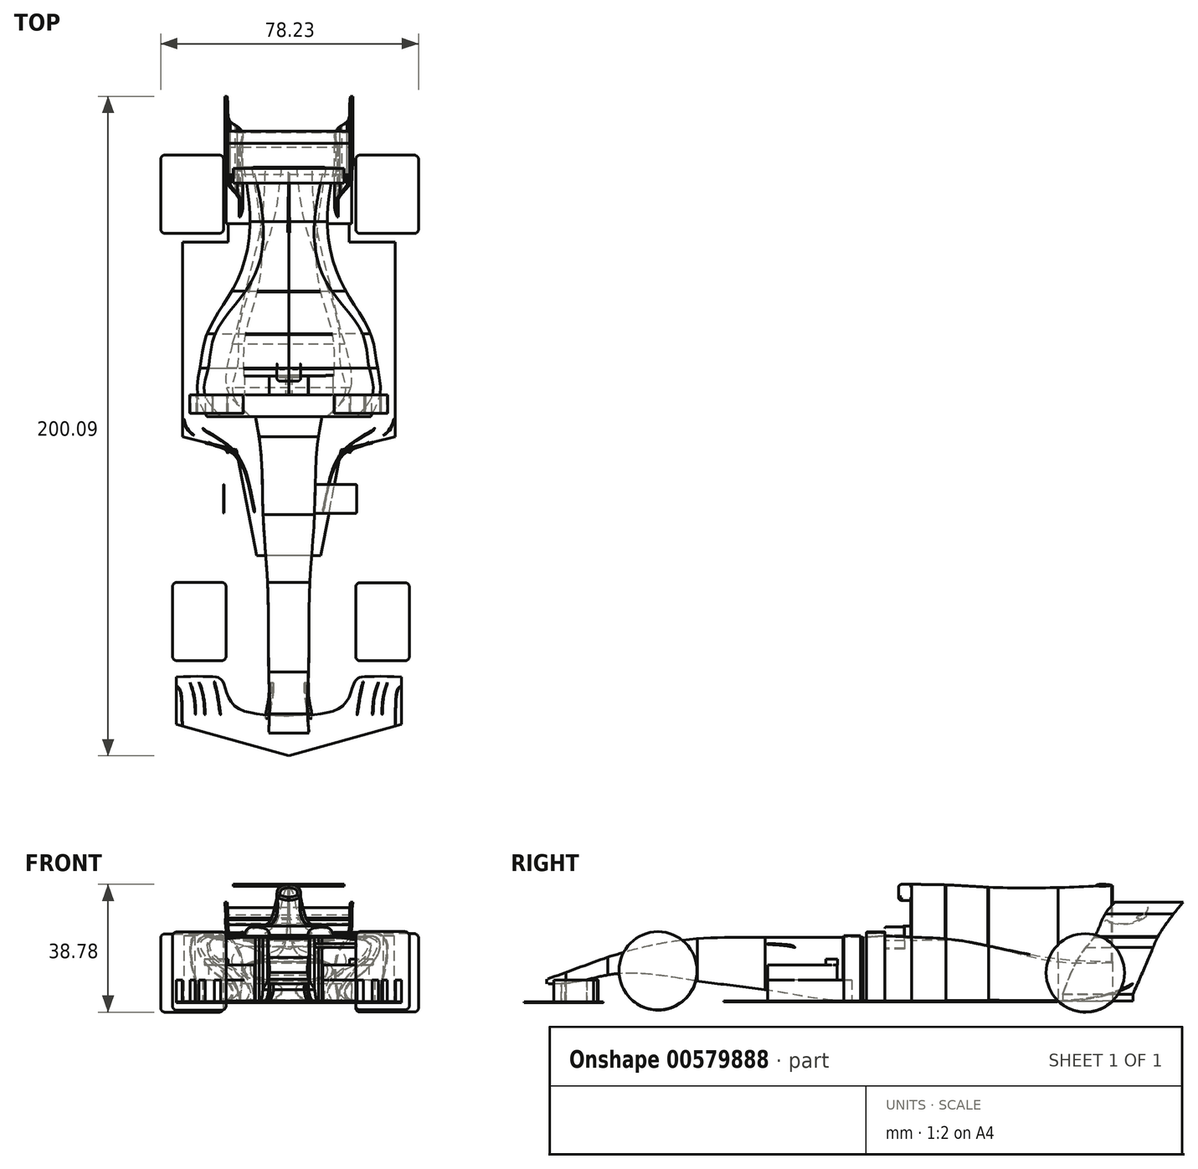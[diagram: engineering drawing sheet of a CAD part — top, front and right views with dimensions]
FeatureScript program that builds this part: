
annotation { "Feature Type Name" : "Feature", "Feature Type Description" : "" }
export const myFeature = defineFeature(function(context is Context, id is Id, definition is map)
    precondition{}
    {
        {
            var Q0;
            Q0=qCreatedBy(makeId("Top.planeOp"),FACE);
            cPlane(context, id + "F0", {"entities" : qUnion([Q0]), "cplaneType" : CPlaneType.OFFSET, "offset" : 1.52 * mm, "width" : 152.4 * mm, "height" : 152.4 * mm});
        }
        {
            var Q0;
            Q0=qCreatedBy(id+"F0.planeOp",FACE);
            var sketch = newSketch(context, id + "F1", { "sketchPlane" : qUnion([Q0])});
            skLineSegment(sketch, "E0", {"start": v(0, -36.14) * mm, "end": v(9.74, -36.14) * mm});
            skLineSegment(sketch, "E1", {"start": v(9.74, -36.14) * mm, "end": v(15.88, -3.95) * mm});
            skLineSegment(sketch, "E2", {"start": v(15.88, -3.95) * mm, "end": v(32.24, 0) * mm});
            skLineSegment(sketch, "E3", {"start": v(32.24, 0) * mm, "end": v(32.24, 59.05) * mm});
            skLineSegment(sketch, "E4", {"start": v(32.24, 59.05) * mm, "end": v(18.33, 59.05) * mm});
            skLineSegment(sketch, "E5", {"start": v(18.33, 59.05) * mm, "end": v(18.33, 64.56) * mm});
            skLineSegment(sketch, "E6", {"start": v(18.33, 64.56) * mm, "end": v(0, 64.56) * mm});
            skLineSegment(sketch, "E7.MirrorCS", {"start": v(-18.33, 64.56) * mm, "end": v(0, 64.56) * mm});
            skLineSegment(sketch, "E8.MirrorCS", {"start": v(-18.33, 59.05) * mm, "end": v(-18.33, 64.56) * mm});
            skLineSegment(sketch, "E9.MirrorCS", {"start": v(-32.24, 59.05) * mm, "end": v(-18.33, 59.05) * mm});
            skLineSegment(sketch, "E10.MirrorCS", {"start": v(-32.24, 0) * mm, "end": v(-32.24, 59.05) * mm});
            skLineSegment(sketch, "E11.MirrorCS", {"start": v(-15.88, -3.95) * mm, "end": v(-32.24, 0) * mm});
            skLineSegment(sketch, "E12.MirrorCS", {"start": v(-9.74, -36.14) * mm, "end": v(-15.88, -3.95) * mm});
            skLineSegment(sketch, "E13.MirrorCS", {"start": v(0, -36.14) * mm, "end": v(-9.74, -36.14) * mm});
            skSolve(sketch);
        }
        {
            var Q0;
            Q0 = qSketchRegion(id + "F1", true);
            extrude(context, id + "F2", {"entities" : qUnion([Q0]), "depth" : 0.25 * mm, "offsetDistance" : 25.4 * mm});
        }
        {
            var Q0;
            Q0=qCreatedBy(makeId("Front.planeOp"),FACE);
            cPlane(context, id + "F3", {"entities" : qUnion([Q0]), "cplaneType" : CPlaneType.OFFSET, "offset" : 6.1 * mm, "oppositeDirection" : true, "width" : 152.4 * mm, "height" : 152.4 * mm});
        }
        {
            var Q0;
            Q0=qCreatedBy(id+"F3.planeOp",FACE);
            var sketch = newSketch(context, id + "F4", { "sketchPlane" : qUnion([Q0])});
            skLineSegment(sketch, "E14", {"start": v(0, 21.08) * mm, "end": v(-20.66, 21.08) * mm});
            skFitSpline(sketch, "E15", {"points": [v(-20.66, 21.08) * mm, v(-24.08, 20.42) * mm, v(-24.53, 17.17) * mm, v(-20.66, 13.07) * mm, v(-17.24, 11.22) * mm, v(-12.52, 6.88) * mm, v(-11.6, 3.37) * mm, v(-11.6, 1.83) * mm], "startDerivative": vector(-14.07, -2.12) * mm, "endDerivative": vector(0, -19.5) * mm});
            skLineSegment(sketch, "E16", {"start": v(-11.6, 1.83) * mm, "end": v(0, 1.83) * mm});
            skLineSegment(sketch, "E17.MirrorCS", {"start": v(11.6, 1.83) * mm, "end": v(0, 1.83) * mm});
            skFitSpline(sketch, "E18.MirrorCS", {"points": [v(20.66, 21.08) * mm, v(24.08, 20.42) * mm, v(24.53, 17.17) * mm, v(20.66, 13.07) * mm, v(17.24, 11.22) * mm, v(12.52, 6.88) * mm, v(11.6, 3.37) * mm, v(11.6, 1.83) * mm], "startDerivative": vector(14.07, -2.12) * mm, "endDerivative": vector(0, -19.5) * mm});
            skLineSegment(sketch, "E19.MirrorCS", {"start": v(0, 21.08) * mm, "end": v(20.66, 21.08) * mm});
            skSolve(sketch);
        }
        {
            var Q0;
            Q0=qCreatedBy(makeId("Front.planeOp"),FACE);
            cPlane(context, id + "F5", {"entities" : qUnion([Q0]), "cplaneType" : CPlaneType.OFFSET, "offset" : 12.7 * mm, "oppositeDirection" : true, "width" : 152.4 * mm, "height" : 152.4 * mm});
        }
        {
            var Q0;
            Q0=qCreatedBy(id+"F5.planeOp",FACE);
            var sketch = newSketch(context, id + "F6", { "sketchPlane" : qUnion([Q0])});
            skLineSegment(sketch, "E20", {"start": v(0, 21.43) * mm, "end": v(-25.43, 21.43) * mm});
            skFitSpline(sketch, "E21", {"points": [v(-25.43, 21.43) * mm, v(-27.4, 19.99) * mm, v(-26.9, 15.65) * mm, v(-25.16, 13.06) * mm, v(-22.6, 10.51) * mm, v(-17.72, 6.46) * mm, v(-17.04, 3.68) * mm, v(-17.85, 1.8) * mm], "startDerivative": vector(-11.51, -2.68) * mm, "endDerivative": vector(-12.74, -13.46) * mm});
            skLineSegment(sketch, "E22.MirrorCS", {"start": v(0, 21.43) * mm, "end": v(25.43, 21.43) * mm});
            skFitSpline(sketch, "E23.MirrorCS", {"points": [v(25.43, 21.43) * mm, v(27.4, 19.99) * mm, v(26.9, 15.65) * mm, v(25.16, 13.06) * mm, v(22.6, 10.51) * mm, v(17.72, 6.46) * mm, v(17.04, 3.68) * mm, v(17.85, 1.8) * mm], "startDerivative": vector(11.51, -2.68) * mm, "endDerivative": vector(12.74, -13.46) * mm});
            skLineSegment(sketch, "E24", {"start": v(-17.85, 1.8) * mm, "end": v(0, 1.8) * mm});
            skLineSegment(sketch, "E25.MirrorCS", {"start": v(17.85, 1.8) * mm, "end": v(0, 1.8) * mm});
            skSolve(sketch);
        }
        {
            var Q0;
            Q0=qCreatedBy(makeId("Front.planeOp"),FACE);
            cPlane(context, id + "F7", {"entities" : qUnion([Q0]), "cplaneType" : CPlaneType.OFFSET, "offset" : 20.83 * mm, "oppositeDirection" : true, "width" : 152.4 * mm, "height" : 152.4 * mm});
        }
        {
            var Q0;
            Q0=qCreatedBy(id+"F7.planeOp",FACE);
            var sketch = newSketch(context, id + "F8", { "sketchPlane" : qUnion([Q0])});
            skLineSegment(sketch, "E26", {"start": v(0, 21.13) * mm, "end": v(-24.43, 21.13) * mm});
            skFitSpline(sketch, "E27", {"points": [v(-24.43, 21.13) * mm, v(-26.8, 19.6) * mm, v(-25.78, 15.83) * mm, v(-24.43, 14.33) * mm, v(-21.34, 11.76) * mm, v(-17.18, 7.5) * mm, v(-15.86, 3.52) * mm, v(-18.92, 1.72) * mm], "startDerivative": vector(-13.1, -3.81) * mm, "endDerivative": vector(-24.59, -10.93) * mm});
            skLineSegment(sketch, "E28", {"start": v(-18.92, 1.72) * mm, "end": v(0, 1.72) * mm});
            skLineSegment(sketch, "E29.MirrorCS", {"start": v(0, 21.13) * mm, "end": v(24.43, 21.13) * mm});
            skFitSpline(sketch, "E30.MirrorCS", {"points": [v(24.43, 21.13) * mm, v(26.8, 19.6) * mm, v(25.78, 15.83) * mm, v(24.43, 14.33) * mm, v(21.34, 11.76) * mm, v(17.18, 7.5) * mm, v(15.86, 3.52) * mm, v(18.92, 1.72) * mm], "startDerivative": vector(13.1, -3.81) * mm, "endDerivative": vector(24.59, -10.93) * mm});
            skLineSegment(sketch, "E31.MirrorCS", {"start": v(18.92, 1.72) * mm, "end": v(0, 1.72) * mm});
            skSolve(sketch);
        }
        {
            var Q0;
            Q0=qCreatedBy(makeId("Front.planeOp"),FACE);
            cPlane(context, id + "F9", {"entities" : qUnion([Q0]), "cplaneType" : CPlaneType.OFFSET, "offset" : 31.24 * mm, "oppositeDirection" : true, "width" : 152.4 * mm, "height" : 152.4 * mm});
        }
        {
            var Q0;
            Q0=qCreatedBy(id+"F9.planeOp",FACE);
            var sketch = newSketch(context, id + "F10", { "sketchPlane" : qUnion([Q0])});
            skLineSegment(sketch, "E32", {"start": v(0, 20.64) * mm, "end": v(-22.4, 20.64) * mm});
            skFitSpline(sketch, "E33", {"points": [v(-22.4, 20.64) * mm, v(-24.53, 18.88) * mm, v(-24.28, 15.63) * mm, v(-22.8, 13.69) * mm, v(-20.83, 12.1) * mm, v(-16.57, 7.67) * mm, v(-15.37, 3.35) * mm, v(-16.12, 1.82) * mm], "startDerivative": vector(-10.02, -1.64) * mm, "endDerivative": vector(-7.67, -10.3) * mm});
            skLineSegment(sketch, "E34", {"start": v(-16.12, 1.82) * mm, "end": v(0, 1.82) * mm});
            skLineSegment(sketch, "E35.MirrorCS", {"start": v(0, 20.64) * mm, "end": v(22.4, 20.64) * mm});
            skFitSpline(sketch, "E36.MirrorCS", {"points": [v(22.4, 20.64) * mm, v(24.53, 18.88) * mm, v(24.28, 15.63) * mm, v(22.8, 13.69) * mm, v(20.83, 12.1) * mm, v(16.57, 7.67) * mm, v(15.37, 3.35) * mm, v(16.12, 1.82) * mm], "startDerivative": vector(10.02, -1.64) * mm, "endDerivative": vector(7.67, -10.3) * mm});
            skLineSegment(sketch, "E37.MirrorCS", {"start": v(16.12, 1.82) * mm, "end": v(0, 1.82) * mm});
            skSolve(sketch);
        }
        {
            var Q0;
            Q0=qCreatedBy(makeId("Front.planeOp"),FACE);
            cPlane(context, id + "F11", {"entities" : qUnion([Q0]), "cplaneType" : CPlaneType.OFFSET, "offset" : 44.2 * mm, "oppositeDirection" : true, "width" : 152.4 * mm, "height" : 152.4 * mm});
        }
        {
            var Q0;
            Q0=qCreatedBy(makeId("Front.planeOp"),FACE);
            cPlane(context, id + "F12", {"entities" : qUnion([Q0]), "cplaneType" : CPlaneType.OFFSET, "offset" : 65.28 * mm, "oppositeDirection" : true, "width" : 152.4 * mm, "height" : 152.4 * mm});
        }
        {
            var Q0;
            Q0=qCreatedBy(id+"F12.planeOp",FACE);
            var sketch = newSketch(context, id + "F13", { "sketchPlane" : qUnion([Q0])});
            skLineSegment(sketch, "E38", {"start": v(0, 14.58) * mm, "end": v(-7.82, 14.58) * mm});
            skFitSpline(sketch, "E39", {"points": [v(-7.82, 14.58) * mm, v(-11.15, 12.99) * mm, v(-11.62, 10.56) * mm, v(-10.8, 9.03) * mm, v(-7.82, 7.78) * mm, v(-4.75, 6.13) * mm, v(-6.17, 3.06) * mm, v(-8.2, 1.83) * mm], "startDerivative": vector(-13.2, -1) * mm, "endDerivative": vector(-13.85, -8.87) * mm});
            skLineSegment(sketch, "E40", {"start": v(-8.2, 1.83) * mm, "end": v(0, 1.83) * mm});
            skLineSegment(sketch, "E41.MirrorCS", {"start": v(0, 14.58) * mm, "end": v(7.82, 14.58) * mm});
            skFitSpline(sketch, "E42.MirrorCS", {"points": [v(7.82, 14.58) * mm, v(11.15, 12.99) * mm, v(11.62, 10.56) * mm, v(10.8, 9.03) * mm, v(7.82, 7.78) * mm, v(4.75, 6.13) * mm, v(6.17, 3.06) * mm, v(8.2, 1.83) * mm], "startDerivative": vector(13.2, -1) * mm, "endDerivative": vector(13.85, -8.87) * mm});
            skLineSegment(sketch, "E43.MirrorCS", {"start": v(8.2, 1.83) * mm, "end": v(0, 1.83) * mm});
            skSolve(sketch);
        }
        {
            var Q0;
            Q0=qCreatedBy(id+"F11.planeOp",FACE);
            var sketch = newSketch(context, id + "F14", { "sketchPlane" : qUnion([Q0])});
            skLineSegment(sketch, "E44", {"start": v(0, 18.43) * mm, "end": v(-13.07, 18.43) * mm});
            skFitSpline(sketch, "E45", {"points": [v(-13.07, 18.43) * mm, v(-16.95, 15.5) * mm, v(-16.64, 11.23) * mm, v(-14.93, 9.11) * mm, v(-13.61, 7.75) * mm, v(-12.5, 6.19) * mm, v(-12.15, 3.76) * mm, v(-13.04, 1.94) * mm], "startDerivative": vector(-21.24, 0.66) * mm, "endDerivative": vector(-6.74, -11.7) * mm});
            skLineSegment(sketch, "E46", {"start": v(-13.04, 1.94) * mm, "end": v(0, 1.94) * mm});
            skFitSpline(sketch, "E47.MirrorCS", {"points": [v(13.07, 18.43) * mm, v(16.95, 15.5) * mm, v(16.64, 11.23) * mm, v(14.93, 9.11) * mm, v(13.61, 7.75) * mm, v(12.5, 6.19) * mm, v(12.15, 3.76) * mm, v(13.04, 1.94) * mm], "startDerivative": vector(21.24, 0.66) * mm, "endDerivative": vector(6.74, -11.7) * mm});
            skLineSegment(sketch, "E48.MirrorCS", {"start": v(0, 18.43) * mm, "end": v(13.07, 18.43) * mm});
            skLineSegment(sketch, "E49.MirrorCS", {"start": v(13.04, 1.94) * mm, "end": v(0, 1.94) * mm});
            skSolve(sketch);
        }
        {
            var Q0;
            Q0=qCreatedBy(makeId("Front.planeOp"),FACE);
            cPlane(context, id + "F15", {"entities" : qUnion([Q0]), "cplaneType" : CPlaneType.OFFSET, "offset" : 81.8 * mm, "oppositeDirection" : true, "width" : 152.4 * mm, "height" : 152.4 * mm});
        }
        {
            var Q0;
            Q0=qCreatedBy(id+"F15.planeOp",FACE);
            var sketch = newSketch(context, id + "F16", { "sketchPlane" : qUnion([Q0])});
            skLineSegment(sketch, "E50", {"start": v(0, 13.69) * mm, "end": v(-10.77, 13.69) * mm});
            skFitSpline(sketch, "E51", {"points": [v(-10.77, 13.69) * mm, v(-12.3, 13.22) * mm, v(-13.7, 11.27) * mm, v(-12.76, 9.24) * mm, v(-10.22, 8.52) * mm, v(-3.54, 7.08) * mm, v(-2.77, 3.5) * mm, v(-7.08, 1.82) * mm], "startDerivative": vector(-13.13, -1.96) * mm, "endDerivative": vector(-9.84, -12.7) * mm});
            skLineSegment(sketch, "E52", {"start": v(-7.08, 1.82) * mm, "end": v(0, 1.82) * mm});
            skLineSegment(sketch, "E53.MirrorCS", {"start": v(0, 13.69) * mm, "end": v(10.77, 13.69) * mm});
            skFitSpline(sketch, "E54.MirrorCS", {"points": [v(10.77, 13.69) * mm, v(12.3, 13.22) * mm, v(13.7, 11.27) * mm, v(12.76, 9.24) * mm, v(10.22, 8.52) * mm, v(3.54, 7.08) * mm, v(2.77, 3.5) * mm, v(7.08, 1.82) * mm], "startDerivative": vector(13.13, -1.96) * mm, "endDerivative": vector(9.84, -12.7) * mm});
            skLineSegment(sketch, "E55.MirrorCS", {"start": v(7.08, 1.82) * mm, "end": v(0, 1.82) * mm});
            skSolve(sketch);
        }
        {
            var Q0;
            Q0 = qSketchRegion(id + "F16", true);
            var Q1;
            Q1 = qSketchRegion(id + "F14", true);
            var Q2;
            Q2 = qSketchRegion(id + "F13", true);
            var Q3;
            Q3 = qSketchRegion(id + "F10", true);
            var Q4;
            Q4 = qSketchRegion(id + "F8", true);
            var Q5;
            Q5 = qSketchRegion(id + "F6", true);
            var Q6;
            Q6 = qSketchRegion(id + "F4", true);
            extrude(context, id + "F17", {"entities" : qUnion([Q0, Q1, Q2, Q3, Q4, Q5, Q6]), "depth" : 0.03 * mm, "offsetDistance" : 25.4 * mm});
        }
        {
            var Q0;
            Q0=makeQuery(id+"F4.imprint","IMPRINT",FACE,{"disambiguationData":[TD([[makeQuery(id+"F4.imprint","IMPRINT",EDGE,{"derivedFrom":sQuery(id+"F4.wireOp",EDGE,"E14")}),1.0]])]});
            var Q1;
            Q1=makeQuery(id+"F6.imprint","IMPRINT",FACE,{"disambiguationData":[TD([[makeQuery(id+"F6.imprint","IMPRINT",EDGE,{"derivedFrom":sQuery(id+"F6.wireOp",EDGE,"E20")}),1.0]])]});
            var Q2;
            Q2=makeQuery(id+"F8.imprint","IMPRINT",FACE,{"disambiguationData":[TD([[makeQuery(id+"F8.imprint","IMPRINT",EDGE,{"derivedFrom":sQuery(id+"F8.wireOp",EDGE,"E26")}),1.0]])]});
            var Q3;
            Q3=makeQuery(id+"F10.imprint","IMPRINT",FACE,{"disambiguationData":[TD([[makeQuery(id+"F10.imprint","IMPRINT",EDGE,{"derivedFrom":sQuery(id+"F10.wireOp",EDGE,"E32")}),1.0]])]});
            var Q4;
            Q4=makeQuery(id+"F14.imprint","IMPRINT",FACE,{"disambiguationData":[TD([[makeQuery(id+"F14.imprint","IMPRINT",EDGE,{"derivedFrom":sQuery(id+"F14.wireOp",EDGE,"E44")}),1.0]])]});
            var Q5;
            Q5=makeQuery(id+"F13.imprint","IMPRINT",FACE,{"disambiguationData":[TD([[makeQuery(id+"F13.imprint","IMPRINT",EDGE,{"derivedFrom":sQuery(id+"F13.wireOp",EDGE,"E38")}),1.0]])]});
            var Q6;
            Q6=makeQuery(id+"F16.imprint","IMPRINT",FACE,{"disambiguationData":[TD([[makeQuery(id+"F16.imprint","IMPRINT",EDGE,{"derivedFrom":sQuery(id+"F16.wireOp",EDGE,"E50")}),1.0]])]});
            loft(context, id + "F18", {"sheetProfilesArray" : [{ "sheetProfileEntities" : qUnion([Q0]) }, { "sheetProfileEntities" : qUnion([Q1]) }, { "sheetProfileEntities" : qUnion([Q2]) }, { "sheetProfileEntities" : qUnion([Q3]) }, { "sheetProfileEntities" : qUnion([Q4]) }, { "sheetProfileEntities" : qUnion([Q5]) }, { "sheetProfileEntities" : qUnion([Q6]) }]});
        }
        {
            var Q0;
            Q0=qCreatedBy(makeId("Right.planeOp"),FACE);
            cPlane(context, id + "F19", {"entities" : qUnion([Q0]), "cplaneType" : CPlaneType.OFFSET, "offset" : 20.32 * mm, "width" : 152.4 * mm, "height" : 152.4 * mm});
        }
        {
            var Q0;
            Q0=qCreatedBy(makeId("Right.planeOp"),FACE);
            cPlane(context, id + "F20", {"entities" : qUnion([Q0]), "cplaneType" : CPlaneType.OFFSET, "offset" : 19.8 * mm, "oppositeDirection" : true, "width" : 152.4 * mm, "height" : 152.4 * mm});
        }
        {
            var Q0;
            Q0=qCreatedBy(id+"F19.planeOp",FACE);
            var sketch = newSketch(context, id + "F21", { "sketchPlane" : qUnion([Q0])});
            skCircle(sketch, "E56", {"center": v(73.53, 10.3) * mm, "radius": 11.88 * mm});
            skSolve(sketch);
        }
        {
            var Q0;
            Q0=qCreatedBy(id+"F20.planeOp",FACE);
            var sketch = newSketch(context, id + "F22", { "sketchPlane" : qUnion([Q0])});
            skCircle(sketch, "E57", {"center": v(73.58, 10.23) * mm, "radius": 11.86 * mm});
            skSolve(sketch);
        }
        {
            var Q0;
            Q0 = qSketchRegion(id + "F22", true);
            extrude(context, id + "F23", {"entities" : qUnion([Q0]), "oppositeDirection" : true, "depth" : 19.05 * mm, "offsetDistance" : 25.4 * mm});
        }
        {
            var Q0;
            Q0=makeQuery(id+"F21.imprint","IMPRINT",FACE,{"disambiguationData":[TD([[makeQuery(id+"F21.imprint","IMPRINT",EDGE,{"derivedFrom":sQuery(id+"F21.wireOp",EDGE,"E56")}),1.0]])]});
            extrude(context, id + "F24", {"entities" : qUnion([Q0]), "depth" : 19.05 * mm, "offsetDistance" : 25.4 * mm});
        }
        {
            var Q0;
            Q0=qCreatedBy(id+"F5.planeOp",FACE);
            var sketch = newSketch(context, id + "F25", { "sketchPlane" : qUnion([Q0])});
            skLineSegment(sketch, "E58", {"start": v(-14.07, 21.3) * mm, "end": v(-14.07, 22.26) * mm});
            skLineSegment(sketch, "E59", {"start": v(-14.07, 21.3) * mm, "end": v(-13.76, 21.3) * mm});
            skLineSegment(sketch, "E60", {"start": v(-13.76, 21.3) * mm, "end": v(-13.76, 22.26) * mm});
            skLineSegment(sketch, "E61", {"start": v(-14.07, 22.26) * mm, "end": v(-18.39, 22.26) * mm});
            skLineSegment(sketch, "E62", {"start": v(-18.39, 22.26) * mm, "end": v(-18.39, 21.15) * mm});
            skLineSegment(sketch, "E63", {"start": v(-18.39, 21.15) * mm, "end": v(-18.72, 21.15) * mm});
            skLineSegment(sketch, "E64", {"start": v(-18.72, 21.15) * mm, "end": v(-18.72, 22.26) * mm});
            skLineSegment(sketch, "E65", {"start": v(-18.72, 22.26) * mm, "end": v(-22.91, 22.26) * mm});
            skLineSegment(sketch, "E66", {"start": v(-22.91, 22.26) * mm, "end": v(-22.91, 21.15) * mm});
            skLineSegment(sketch, "E67", {"start": v(-22.91, 21.15) * mm, "end": v(-23.25, 21.15) * mm});
            skLineSegment(sketch, "E68", {"start": v(-23.25, 21.15) * mm, "end": v(-23.25, 22.26) * mm});
            skLineSegment(sketch, "E69", {"start": v(-23.25, 22.26) * mm, "end": v(-25.19, 22.26) * mm});
            skFitSpline(sketch, "E70", {"points": [v(-13.76, 22.26) * mm, v(-13.89, 22.61) * mm, v(-14.18, 22.63) * mm, v(-17, 22.6) * mm, v(-25.25, 22.6) * mm, v(-26.09, 22.58) * mm, v(-26.89, 22.47) * mm, v(-27.43, 22.26) * mm, v(-28.64, 21.5) * mm, v(-29.89, 19.12) * mm, v(-29.92, 16.38) * mm, v(-29.53, 12.69) * mm, v(-28.55, 8.5) * mm, v(-27.98, 4.57) * mm, v(-28.07, 1.78) * mm], "startDerivative": vector(-5.07, 15.17) * mm, "endDerivative": vector(-2.51, -33.45) * mm});
            skFitSpline(sketch, "E71", {"points": [v(-25.19, 22.26) * mm, v(-25.88, 22.26) * mm, v(-27.32, 21.92) * mm, v(-28.28, 21.35) * mm, v(-29.14, 20.12) * mm, v(-29.62, 18.68) * mm, v(-29.6, 16.32) * mm, v(-29.17, 12.69) * mm, v(-28.34, 8.97) * mm, v(-27.77, 6.04) * mm, v(-27.65, 3.07) * mm, v(-27.7, 1.75) * mm], "startDerivative": vector(-11.42, 0.46) * mm, "endDerivative": vector(-1.02, -15.85) * mm});
            skLineSegment(sketch, "E72", {"start": v(-28.07, 1.78) * mm, "end": v(-27.7, 1.75) * mm});
            skFitSpline(sketch, "E73.MirrorCS", {"points": [v(13.76, 22.26) * mm, v(13.89, 22.61) * mm, v(14.18, 22.63) * mm, v(17, 22.6) * mm, v(25.25, 22.6) * mm, v(26.09, 22.58) * mm, v(26.89, 22.47) * mm, v(27.43, 22.26) * mm, v(28.64, 21.5) * mm, v(29.89, 19.12) * mm, v(29.92, 16.38) * mm, v(29.53, 12.69) * mm, v(28.55, 8.5) * mm, v(27.98, 4.57) * mm, v(28.07, 1.78) * mm], "startDerivative": vector(5.07, 15.17) * mm, "endDerivative": vector(2.51, -33.45) * mm});
            skLineSegment(sketch, "E74.MirrorCS", {"start": v(14.07, 22.26) * mm, "end": v(18.39, 22.26) * mm});
            skLineSegment(sketch, "E75.MirrorCS", {"start": v(14.07, 21.3) * mm, "end": v(14.07, 22.26) * mm});
            skLineSegment(sketch, "E76.MirrorCS", {"start": v(13.76, 21.3) * mm, "end": v(13.76, 22.26) * mm});
            skLineSegment(sketch, "E77.MirrorCS", {"start": v(14.07, 21.3) * mm, "end": v(13.76, 21.3) * mm});
            skLineSegment(sketch, "E78.MirrorCS", {"start": v(18.39, 22.26) * mm, "end": v(18.39, 21.15) * mm});
            skLineSegment(sketch, "E79.MirrorCS", {"start": v(18.39, 21.15) * mm, "end": v(18.72, 21.15) * mm});
            skLineSegment(sketch, "E80.MirrorCS", {"start": v(18.72, 21.15) * mm, "end": v(18.72, 22.26) * mm});
            skLineSegment(sketch, "E81.MirrorCS", {"start": v(18.72, 22.26) * mm, "end": v(22.91, 22.26) * mm});
            skFitSpline(sketch, "E82.MirrorCS", {"points": [v(25.19, 22.26) * mm, v(25.88, 22.26) * mm, v(27.32, 21.92) * mm, v(28.28, 21.35) * mm, v(29.14, 20.12) * mm, v(29.62, 18.68) * mm, v(29.6, 16.32) * mm, v(29.17, 12.69) * mm, v(28.34, 8.97) * mm, v(27.77, 6.04) * mm, v(27.65, 3.07) * mm, v(27.7, 1.75) * mm], "startDerivative": vector(11.42, 0.46) * mm, "endDerivative": vector(1.02, -15.85) * mm});
            skLineSegment(sketch, "E83.MirrorCS", {"start": v(23.25, 22.26) * mm, "end": v(25.19, 22.26) * mm});
            skLineSegment(sketch, "E84.MirrorCS", {"start": v(23.25, 21.15) * mm, "end": v(23.25, 22.26) * mm});
            skLineSegment(sketch, "E85.MirrorCS", {"start": v(22.91, 22.26) * mm, "end": v(22.91, 21.15) * mm});
            skLineSegment(sketch, "E86.MirrorCS", {"start": v(22.91, 21.15) * mm, "end": v(23.25, 21.15) * mm});
            skLineSegment(sketch, "E87.MirrorCS", {"start": v(-11.56, 1.78) * mm, "end": v(-11.92, 1.75) * mm});
            skLineSegment(sketch, "E88", {"start": v(27.7, 1.75) * mm, "end": v(28.07, 1.78) * mm});
            skSolve(sketch);
        }
        {
            var Q0;
            Q0 = qSketchRegion(id + "F25", true);
            extrude(context, id + "F26", {"entities" : qUnion([Q0]), "operationType" : NewBodyOperationType.ADD, "depth" : 5.6 * mm, "offsetDistance" : 25.4 * mm});
        }
        {
            var Q0;
            Q0=makeQuery(id+"F24.opExtrude","CAP_EDGE",EDGE,{"disambiguationData":[OSD([sQuery(id+"F21.wireOp",EDGE,"E56")])],"isStart":false});
            fillet(context, id + "F27", {"entities" : qUnion([Q0]), "radius" : 1.27 * mm, "tangentPropagation" : true, "allowEdgeOverflow" : false});
        }
        {
            var Q0;
            Q0=makeQuery(id+"F24.opExtrude","CAP_EDGE",EDGE,{"disambiguationData":[OSD([sQuery(id+"F21.wireOp",EDGE,"E56")])],"isStart":true});
            fillet(context, id + "F28", {"entities" : qUnion([Q0]), "radius" : 1.27 * mm, "tangentPropagation" : true, "allowEdgeOverflow" : false});
        }
        {
            var Q0;
            Q0=makeQuery(id+"F23.opExtrude","CAP_EDGE",EDGE,{"disambiguationData":[OSD([sQuery(id+"F22.wireOp",EDGE,"E57")])],"isStart":true});
            fillet(context, id + "F29", {"entities" : qUnion([Q0]), "radius" : 1.27 * mm, "tangentPropagation" : true, "allowEdgeOverflow" : false});
        }
        {
            var Q0;
            Q0=makeQuery(id+"F23.opExtrude","CAP_EDGE",EDGE,{"disambiguationData":[OSD([sQuery(id+"F22.wireOp",EDGE,"E57")])],"isStart":false});
            fillet(context, id + "F30", {"entities" : qUnion([Q0]), "radius" : 1.27 * mm, "tangentPropagation" : true, "allowEdgeOverflow" : false});
        }
        {
            var Q0;
            Q0=makeQuery(id+"F2.opExtrude","CAP_FACE",FACE,{"disambiguationData":[OSD([sQuery(id+"F1.wireOp",EDGE,"E0"),sQuery(id+"F1.wireOp",EDGE,"E1"),sQuery(id+"F1.wireOp",EDGE,"E2"),sQuery(id+"F1.wireOp",EDGE,"E3"),sQuery(id+"F1.wireOp",EDGE,"E4"),sQuery(id+"F1.wireOp",EDGE,"E5"),sQuery(id+"F1.wireOp",EDGE,"E6"),sQuery(id+"F1.wireOp",EDGE,"E7.MirrorCS"),sQuery(id+"F1.wireOp",EDGE,"E8.MirrorCS"),sQuery(id+"F1.wireOp",EDGE,"E9.MirrorCS"),sQuery(id+"F1.wireOp",EDGE,"E10.MirrorCS"),sQuery(id+"F1.wireOp",EDGE,"E11.MirrorCS"),sQuery(id+"F1.wireOp",EDGE,"E12.MirrorCS"),sQuery(id+"F1.wireOp",EDGE,"E13.MirrorCS")])],"isStart":false});
            var sketch = newSketch(context, id + "F31", { "sketchPlane" : qUnion([Q0])});
            skLineSegment(sketch, "E89", {"start": v(-15.07, 66.68) * mm, "end": v(-15.07, 87.96) * mm});
            skLineSegment(sketch, "E90", {"start": v(-15.07, 87.96) * mm, "end": v(-14.7, 87.96) * mm});
            skLineSegment(sketch, "E91", {"start": v(-14.7, 87.96) * mm, "end": v(-14.7, 66.68) * mm});
            skLineSegment(sketch, "E92", {"start": v(-14.7, 66.68) * mm, "end": v(-15.07, 66.68) * mm});
            skLineSegment(sketch, "E93.MirrorCS", {"start": v(15.07, 66.68) * mm, "end": v(15.07, 87.96) * mm});
            skLineSegment(sketch, "E94.MirrorCS", {"start": v(14.7, 87.96) * mm, "end": v(14.7, 66.68) * mm});
            skLineSegment(sketch, "E95.MirrorCS", {"start": v(15.07, 87.96) * mm, "end": v(14.7, 87.96) * mm});
            skLineSegment(sketch, "E96.MirrorCS", {"start": v(14.7, 66.68) * mm, "end": v(15.07, 66.68) * mm});
            skSolve(sketch);
        }
        {
            var Q0;
            Q0 = qSketchRegion(id + "F31", true);
            extrude(context, id + "F32", {"entities" : qUnion([Q0]), "operationType" : NewBodyOperationType.ADD, "depth" : 2.03 * mm, "offsetDistance" : 25.4 * mm});
        }
        {
            var Q0;
            Q0=qCreatedBy(makeId("Top.planeOp"),FACE);
            cPlane(context, id + "F33", {"entities" : qUnion([Q0]), "cplaneType" : CPlaneType.OFFSET, "offset" : 18.03 * mm, "width" : 152.4 * mm, "height" : 152.4 * mm});
        }
        {
            var Q0;
            Q0=qCreatedBy(makeId("Top.planeOp"),FACE);
            cPlane(context, id + "F34", {"entities" : qUnion([Q0]), "cplaneType" : CPlaneType.OFFSET, "offset" : 21.34 * mm, "width" : 152.4 * mm, "height" : 152.4 * mm});
        }
        {
            var Q0;
            Q0=qCreatedBy(makeId("Top.planeOp"),FACE);
            cPlane(context, id + "F35", {"entities" : qUnion([Q0]), "cplaneType" : CPlaneType.OFFSET, "offset" : 28.2 * mm, "width" : 152.4 * mm, "height" : 152.4 * mm});
        }
        {
            var Q0;
            Q0=qCreatedBy(id+"F33.planeOp",FACE);
            var sketch = newSketch(context, id + "F36", { "sketchPlane" : qUnion([Q0])});
            skLineSegment(sketch, "E97", {"start": v(-15.6, 73.75) * mm, "end": v(-15.6, 94.13) * mm});
            skLineSegment(sketch, "E98", {"start": v(-16.16, 73.75) * mm, "end": v(-15.6, 73.75) * mm});
            skLineSegment(sketch, "E99", {"start": v(-16.16, 73.75) * mm, "end": v(-16.16, 94.13) * mm});
            skLineSegment(sketch, "E100", {"start": v(-15.6, 94.13) * mm, "end": v(-16.16, 94.13) * mm});
            skLineSegment(sketch, "E101.MirrorCS", {"start": v(16.16, 73.75) * mm, "end": v(16.16, 94.13) * mm});
            skLineSegment(sketch, "E102.MirrorCS", {"start": v(15.6, 73.75) * mm, "end": v(15.6, 94.13) * mm});
            skLineSegment(sketch, "E103.MirrorCS", {"start": v(15.6, 94.13) * mm, "end": v(16.16, 94.13) * mm});
            skLineSegment(sketch, "E104.MirrorCS", {"start": v(16.16, 73.75) * mm, "end": v(15.6, 73.75) * mm});
            skSolve(sketch);
        }
        {
            var Q0;
            Q0 = qSketchRegion(id + "F36", true);
            extrude(context, id + "F37", {"entities" : qUnion([Q0]), "oppositeDirection" : true, "depth" : 0.03 * mm, "offsetDistance" : 25.4 * mm});
        }
        {
            var Q0;
            Q0=qCreatedBy(id+"F34.planeOp",FACE);
            var sketch = newSketch(context, id + "F38", { "sketchPlane" : qUnion([Q0])});
            skLineSegment(sketch, "E105", {"start": v(-17.72, 76.4) * mm, "end": v(-18.44, 76.4) * mm});
            skLineSegment(sketch, "E106", {"start": v(-17.72, 76.4) * mm, "end": v(-17.72, 95.6) * mm});
            skLineSegment(sketch, "E107", {"start": v(-18.47, 95.6) * mm, "end": v(-17.72, 95.6) * mm});
            skLineSegment(sketch, "E108", {"start": v(-18.47, 95.6) * mm, "end": v(-18.44, 76.4) * mm});
            skLineSegment(sketch, "E109.MirrorCS", {"start": v(18.47, 95.6) * mm, "end": v(18.44, 76.4) * mm});
            skLineSegment(sketch, "E110.MirrorCS", {"start": v(17.72, 76.4) * mm, "end": v(17.72, 95.6) * mm});
            skLineSegment(sketch, "E111.MirrorCS", {"start": v(18.47, 95.6) * mm, "end": v(17.72, 95.6) * mm});
            skLineSegment(sketch, "E112.MirrorCS", {"start": v(17.72, 76.4) * mm, "end": v(18.44, 76.4) * mm});
            skSolve(sketch);
        }
        {
            var Q0;
            Q0 = qSketchRegion(id + "F38", true);
            extrude(context, id + "F39", {"entities" : qUnion([Q0]), "oppositeDirection" : true, "depth" : 0.25 * mm, "offsetDistance" : 25.4 * mm});
        }
        {
            var Q0;
            Q0=qCreatedBy(id+"F35.planeOp",FACE);
            var sketch = newSketch(context, id + "F40", { "sketchPlane" : qUnion([Q0])});
            skLineSegment(sketch, "E113", {"start": v(-19.18, 79.55) * mm, "end": v(-18.47, 79.55) * mm});
            skLineSegment(sketch, "E114", {"start": v(-18.47, 79.55) * mm, "end": v(-18.47, 100.35) * mm});
            skLineSegment(sketch, "E115", {"start": v(-18.47, 100.35) * mm, "end": v(-19.04, 100.35) * mm});
            skLineSegment(sketch, "E116", {"start": v(-19.04, 100.35) * mm, "end": v(-19.18, 79.55) * mm});
            skLineSegment(sketch, "E117.MirrorCS", {"start": v(19.04, 100.35) * mm, "end": v(19.18, 79.55) * mm});
            skLineSegment(sketch, "E118.MirrorCS", {"start": v(18.47, 79.55) * mm, "end": v(18.47, 100.35) * mm});
            skLineSegment(sketch, "E119.MirrorCS", {"start": v(18.47, 100.35) * mm, "end": v(19.04, 100.35) * mm});
            skLineSegment(sketch, "E120.MirrorCS", {"start": v(19.18, 79.55) * mm, "end": v(18.47, 79.55) * mm});
            skSolve(sketch);
        }
        {
            var Q0;
            Q0 = qSketchRegion(id + "F40", true);
            extrude(context, id + "F41", {"entities" : qUnion([Q0]), "oppositeDirection" : true, "depth" : 0.03 * mm, "offsetDistance" : 25.4 * mm});
        }
        {
            var Q0;
            Q0=qCreatedBy(makeId("Right.planeOp"),FACE);
            cPlane(context, id + "F42", {"entities" : qUnion([Q0]), "cplaneType" : CPlaneType.OFFSET, "offset" : 19.05 * mm, "oppositeDirection" : true, "width" : 152.4 * mm, "height" : 152.4 * mm});
        }
        {
            var Q0;
            Q0=qCreatedBy(id+"F42.planeOp",FACE);
            var sketch = newSketch(context, id + "F43", { "sketchPlane" : qUnion([Q0])});
            skFitSpline(sketch, "E121", {"points": [v(79.72, 25.92) * mm, v(79.48, 26.13) * mm, v(79.57, 26.33) * mm, v(79.83, 26.37) * mm, v(80.49, 26.1) * mm, v(81.36, 25.8) * mm, v(83.23, 25.36) * mm, v(86.13, 25.33) * mm, v(87.67, 25.63) * mm, v(91.21, 27.08) * mm, v(92.19, 27.76) * mm, v(92.11, 27.44) * mm, v(90.46, 26.26) * mm, v(88.41, 25.46) * mm, v(86.37, 25) * mm, v(83.05, 24.99) * mm, v(80.22, 25.68) * mm, v(79.72, 25.92) * mm]});
            skFitSpline(sketch, "E122", {"points": [v(90.8, 27.94) * mm, v(89.1, 27.16) * mm, v(89.03, 26.95) * mm, v(89.31, 26.9) * mm, v(89.94, 27.05) * mm, v(90.57, 27.3) * mm, v(91.51, 28) * mm, v(92.37, 29.12) * mm, v(92.64, 29.8) * mm, v(92.62, 30.08) * mm, v(92.4, 29.97) * mm, v(92.28, 29.78) * mm, v(90.8, 27.94) * mm]});
            skSolve(sketch);
        }
        {
            var Q0;
            Q0 = qSketchRegion(id + "F43", true);
            extrude(context, id + "F44", {"entities" : qUnion([Q0]), "depth" : 38.15 * mm, "offsetDistance" : 25.4 * mm});
        }
        {
            var Q0;
            Q0=qCreatedBy(id+"F7.planeOp",FACE);
            var sketch = newSketch(context, id + "F45", { "sketchPlane" : qUnion([Q0])});
            skFitSpline(sketch, "E123", {"points": [v(-13.78, 20) * mm, v(-12.44, 23.67) * mm, v(-5.54, 25.03) * mm, v(-3.54, 32.27) * mm, v(0.06, 37.14) * mm], "startDerivative": vector(5.54, 13.24) * mm, "endDerivative": vector(49.3, 3.23) * mm});
            skLineSegment(sketch, "E124", {"start": v(-13.78, 20) * mm, "end": v(0.09, 20) * mm});
            skFitSpline(sketch, "E125.MirrorCS", {"points": [v(13.78, 20) * mm, v(12.44, 23.67) * mm, v(5.54, 25.03) * mm, v(3.54, 32.27) * mm, v(-0.06, 37.14) * mm], "startDerivative": vector(-5.54, 13.24) * mm, "endDerivative": vector(-49.3, 3.23) * mm});
            skLineSegment(sketch, "E126.MirrorCS", {"start": v(13.78, 20) * mm, "end": v(-0.09, 20) * mm});
            skSolve(sketch);
        }
        {
            var Q0;
            Q0=qCreatedBy(id+"F9.planeOp",FACE);
            var sketch = newSketch(context, id + "F46", { "sketchPlane" : qUnion([Q0])});
            skLineSegment(sketch, "E127", {"start": v(-13.2, 20.14) * mm, "end": v(0, 20.14) * mm});
            skFitSpline(sketch, "E128", {"points": [v(-13.2, 20.14) * mm, v(-12.06, 23.15) * mm, v(-6.31, 25.33) * mm, v(-2.93, 34.94) * mm, v(0.05, 36.99) * mm], "startDerivative": vector(4.36, 13.73) * mm, "endDerivative": vector(15.44, 0.81) * mm});
            skFitSpline(sketch, "E129.MirrorCS", {"points": [v(13.2, 20.14) * mm, v(12.06, 23.15) * mm, v(6.31, 25.33) * mm, v(2.93, 34.94) * mm, v(-0.05, 36.99) * mm], "startDerivative": vector(-4.36, 13.73) * mm, "endDerivative": vector(-15.44, 0.81) * mm});
            skLineSegment(sketch, "E130.MirrorCS", {"start": v(13.2, 20.14) * mm, "end": v(0, 20.14) * mm});
            skSolve(sketch);
        }
        {
            var Q0;
            Q0=qCreatedBy(id+"F11.planeOp",FACE);
            var sketch = newSketch(context, id + "F47", { "sketchPlane" : qUnion([Q0])});
            skLineSegment(sketch, "E131", {"start": v(-9.6, 18.32) * mm, "end": v(0.02, 18.32) * mm});
            skFitSpline(sketch, "E132", {"points": [v(-9.6, 18.32) * mm, v(-7.06, 22.29) * mm, v(-4.17, 24.78) * mm, v(-1.71, 33.12) * mm, v(0.05, 36.3) * mm], "startDerivative": vector(26.07, 15.07) * mm, "endDerivative": vector(11.26, 0.63) * mm});
            skFitSpline(sketch, "E133.MirrorCS", {"points": [v(9.6, 18.32) * mm, v(7.06, 22.29) * mm, v(4.17, 24.78) * mm, v(1.71, 33.12) * mm, v(-0.05, 36.3) * mm], "startDerivative": vector(-26.07, 15.07) * mm, "endDerivative": vector(-11.26, 0.63) * mm});
            skLineSegment(sketch, "E134.MirrorCS", {"start": v(9.6, 18.32) * mm, "end": v(-0.02, 18.32) * mm});
            skSolve(sketch);
        }
        {
            var Q0;
            Q0=qCreatedBy(id+"F15.planeOp",FACE);
            var sketch = newSketch(context, id + "F48", { "sketchPlane" : qUnion([Q0])});
            skLineSegment(sketch, "E135", {"start": v(-11.25, 13.34) * mm, "end": v(0.03, 13.34) * mm});
            skFitSpline(sketch, "E136", {"points": [v(-11.25, 13.34) * mm, v(-4.24, 15.02) * mm, v(-0.65, 21.93) * mm, v(-0.13, 36.15) * mm, v(0.04, 36.81) * mm], "startDerivative": vector(11.52, 12) * mm, "endDerivative": vector(5.85, -2.09) * mm});
            skFitSpline(sketch, "E137.MirrorCS", {"points": [v(11.25, 13.34) * mm, v(4.24, 15.02) * mm, v(0.65, 21.93) * mm, v(0.13, 36.15) * mm, v(-0.04, 36.81) * mm], "startDerivative": vector(-11.52, 12) * mm, "endDerivative": vector(-5.85, -2.09) * mm});
            skLineSegment(sketch, "E138.MirrorCS", {"start": v(11.25, 13.34) * mm, "end": v(-0.03, 13.34) * mm});
            skFitSpline(sketch, "E139.MirrorCS", {"points": [v(11.25, 13.34) * mm, v(4.24, 15.02) * mm, v(0.65, 21.93) * mm, v(0.13, 36.15) * mm, v(-0.04, 36.81) * mm], "startDerivative": vector(-11.52, 12) * mm, "endDerivative": vector(-5.85, -2.09) * mm});
            skFitSpline(sketch, "E140.MirrorCS", {"points": [v(11.25, 13.34) * mm, v(4.24, 15.02) * mm, v(0.65, 21.93) * mm, v(0.13, 36.15) * mm, v(-0.04, 36.81) * mm], "startDerivative": vector(-11.52, 12) * mm, "endDerivative": vector(-5.85, -2.09) * mm});
            skFitSpline(sketch, "E141.MirrorCS", {"points": [v(11.25, 13.34) * mm, v(4.24, 15.02) * mm, v(0.65, 21.93) * mm, v(0.13, 36.15) * mm, v(-0.04, 36.81) * mm], "startDerivative": vector(-11.52, 12) * mm, "endDerivative": vector(-5.85, -2.09) * mm});
            skFitSpline(sketch, "E142.MirrorCS", {"points": [v(11.25, 13.34) * mm, v(4.24, 15.02) * mm, v(0.65, 21.93) * mm, v(0.13, 36.15) * mm, v(-0.04, 36.81) * mm], "startDerivative": vector(-11.52, 12) * mm, "endDerivative": vector(-5.85, -2.09) * mm});
            skSolve(sketch);
        }
        {
            var Q0;
            Q0 = qSketchRegion(id + "F45", true);
            var Q1;
            Q1 = qSketchRegion(id + "F46", true);
            var Q2;
            Q2 = qSketchRegion(id + "F47", true);
            var Q3;
            Q3 = qSketchRegion(id + "F48", true);
            extrude(context, id + "F49", {"entities" : qUnion([Q0, Q1, Q2, Q3]), "depth" : 0.25 * mm, "offsetDistance" : 25.4 * mm});
        }
        {
            var Q0;
            Q0=qCreatedBy(makeId("Top.planeOp"),FACE);
            cPlane(context, id + "F50", {"entities" : qUnion([Q0]), "cplaneType" : CPlaneType.OFFSET, "offset" : 31.75 * mm, "width" : 152.4 * mm, "height" : 152.4 * mm});
        }
        {
            var Q0;
            Q0=qCreatedBy(id+"F50.planeOp",FACE);
            var sketch = newSketch(context, id + "F51", { "sketchPlane" : qUnion([Q0])});
            skLineSegment(sketch, "E143.bottom", {"start": v(-19.45, 82.5) * mm, "end": v(-18.7, 82.5) * mm});
            skLineSegment(sketch, "E143.top", {"start": v(-19.45, 103.27) * mm, "end": v(-18.7, 103.27) * mm});
            skLineSegment(sketch, "E143.left", {"start": v(-19.45, 82.5) * mm, "end": v(-19.45, 103.27) * mm});
            skLineSegment(sketch, "E143.right", {"start": v(-18.7, 82.5) * mm, "end": v(-18.7, 103.27) * mm});
            skLineSegment(sketch, "E144.MirrorCS", {"start": v(18.7, 82.5) * mm, "end": v(18.7, 103.27) * mm});
            skLineSegment(sketch, "E145.MirrorCS", {"start": v(19.45, 82.5) * mm, "end": v(19.45, 103.27) * mm});
            skLineSegment(sketch, "E146.MirrorCS", {"start": v(19.45, 103.27) * mm, "end": v(18.7, 103.27) * mm});
            skLineSegment(sketch, "E147.MirrorCS", {"start": v(19.45, 82.5) * mm, "end": v(18.7, 82.5) * mm});
            skSolve(sketch);
        }
        {
            var Q0;
            Q0 = qSketchRegion(id + "F51", true);
            extrude(context, id + "F52", {"entities" : qUnion([Q0]), "depth" : 0.03 * mm, "offsetDistance" : 25.4 * mm});
        }
        {
            var Q0;
            Q0=makeQuery(id+"F32.opExtrude","CAP_FACE",FACE,{"disambiguationData":[OSD([sQuery(id+"F31.wireOp",EDGE,"E93.MirrorCS"),sQuery(id+"F31.wireOp",EDGE,"E94.MirrorCS"),sQuery(id+"F31.wireOp",EDGE,"E95.MirrorCS"),sQuery(id+"F31.wireOp",EDGE,"E96.MirrorCS")])],"isStart":false});
            var Q1;
            Q1=makeQuery(id+"F37.opExtrude","CAP_FACE",FACE,{"disambiguationData":[OSD([sQuery(id+"F36.wireOp",EDGE,"E101.MirrorCS"),sQuery(id+"F36.wireOp",EDGE,"E102.MirrorCS"),sQuery(id+"F36.wireOp",EDGE,"E103.MirrorCS"),sQuery(id+"F36.wireOp",EDGE,"E104.MirrorCS")])],"isStart":true});
            var Q2;
            Q2=makeQuery(id+"F39.opExtrude","CAP_FACE",FACE,{"disambiguationData":[OSD([sQuery(id+"F38.wireOp",EDGE,"E109.MirrorCS"),sQuery(id+"F38.wireOp",EDGE,"E110.MirrorCS"),sQuery(id+"F38.wireOp",EDGE,"E111.MirrorCS"),sQuery(id+"F38.wireOp",EDGE,"E112.MirrorCS")])],"isStart":true});
            var Q3;
            Q3=makeQuery(id+"F41.opExtrude","CAP_FACE",FACE,{"disambiguationData":[OSD([sQuery(id+"F40.wireOp",EDGE,"E117.MirrorCS"),sQuery(id+"F40.wireOp",EDGE,"E118.MirrorCS"),sQuery(id+"F40.wireOp",EDGE,"E119.MirrorCS"),sQuery(id+"F40.wireOp",EDGE,"E120.MirrorCS")])],"isStart":true});
            var Q4;
            Q4=makeQuery(id+"F52.opExtrude","CAP_FACE",FACE,{"disambiguationData":[OSD([sQuery(id+"F51.wireOp",EDGE,"E144.MirrorCS"),sQuery(id+"F51.wireOp",EDGE,"E145.MirrorCS"),sQuery(id+"F51.wireOp",EDGE,"E146.MirrorCS"),sQuery(id+"F51.wireOp",EDGE,"E147.MirrorCS")])],"isStart":false});
            loft(context, id + "F53", {"sheetProfilesArray" : [{ "sheetProfileEntities" : qUnion([Q0]) }, { "sheetProfileEntities" : qUnion([Q1]) }, { "sheetProfileEntities" : qUnion([Q2]) }, { "sheetProfileEntities" : qUnion([Q3]) }, { "sheetProfileEntities" : qUnion([Q4]) }]});
        }
        {
            var Q0;
            Q0=makeQuery(id+"F52.opExtrude","CAP_FACE",FACE,{"disambiguationData":[OSD([sQuery(id+"F51.wireOp",EDGE,"E143.bottom"),sQuery(id+"F51.wireOp",EDGE,"E143.top"),sQuery(id+"F51.wireOp",EDGE,"E143.left"),sQuery(id+"F51.wireOp",EDGE,"E143.right")])],"isStart":false});
            var Q1;
            Q1=makeQuery(id+"F41.opExtrude","CAP_FACE",FACE,{"disambiguationData":[OSD([sQuery(id+"F40.wireOp",EDGE,"E113"),sQuery(id+"F40.wireOp",EDGE,"E114"),sQuery(id+"F40.wireOp",EDGE,"E115"),sQuery(id+"F40.wireOp",EDGE,"E116")])],"isStart":true});
            var Q2;
            Q2=makeQuery(id+"F39.opExtrude","CAP_FACE",FACE,{"disambiguationData":[OSD([sQuery(id+"F38.wireOp",EDGE,"E105"),sQuery(id+"F38.wireOp",EDGE,"E106"),sQuery(id+"F38.wireOp",EDGE,"E107"),sQuery(id+"F38.wireOp",EDGE,"E108")])],"isStart":true});
            var Q3;
            Q3=makeQuery(id+"F37.opExtrude","CAP_FACE",FACE,{"disambiguationData":[OSD([sQuery(id+"F36.wireOp",EDGE,"E97"),sQuery(id+"F36.wireOp",EDGE,"E98"),sQuery(id+"F36.wireOp",EDGE,"E99"),sQuery(id+"F36.wireOp",EDGE,"E100")])],"isStart":true});
            var Q4;
            Q4=makeQuery(id+"F32.opExtrude","CAP_FACE",FACE,{"disambiguationData":[OSD([sQuery(id+"F31.wireOp",EDGE,"E89"),sQuery(id+"F31.wireOp",EDGE,"E90"),sQuery(id+"F31.wireOp",EDGE,"E91"),sQuery(id+"F31.wireOp",EDGE,"E92")])],"isStart":false});
            loft(context, id + "F54", {"sheetProfilesArray" : [{ "sheetProfileEntities" : qUnion([Q0]) }, { "sheetProfileEntities" : qUnion([Q1]) }, { "sheetProfileEntities" : qUnion([Q2]) }, { "sheetProfileEntities" : qUnion([Q3]) }, { "sheetProfileEntities" : qUnion([Q4]) }]});
        }
        {
            var Q0;
            Q0=qCreatedBy(id+"F12.planeOp",FACE);
            var sketch = newSketch(context, id + "F55", { "sketchPlane" : qUnion([Q0])});
            skLineSegment(sketch, "E148", {"start": v(0.01, 13.55) * mm, "end": v(-8.83, 13.55) * mm});
            skFitSpline(sketch, "E149", {"points": [v(-8.83, 13.55) * mm, v(-3.6, 17.24) * mm, v(-0.81, 22.03) * mm, v(-0.25, 32.92) * mm, v(0.05, 36.18) * mm], "startDerivative": vector(10.73, 30.67) * mm, "endDerivative": vector(5.5, 0) * mm});
            skFitSpline(sketch, "E150.MirrorCS", {"points": [v(8.83, 13.55) * mm, v(3.6, 17.24) * mm, v(0.81, 22.03) * mm, v(0.25, 32.92) * mm, v(-0.05, 36.18) * mm], "startDerivative": vector(-10.73, 30.67) * mm, "endDerivative": vector(-5.5, 0) * mm});
            skLineSegment(sketch, "E151.MirrorCS", {"start": v(-0.01, 13.55) * mm, "end": v(8.83, 13.55) * mm});
            skSolve(sketch);
        }
        {
            var Q0;
            Q0 = qSketchRegion(id + "F55", true);
            extrude(context, id + "F56", {"entities" : qUnion([Q0]), "depth" : 0.03 * mm, "offsetDistance" : 25.4 * mm});
        }
        {
            var Q0;
            Q0=makeQuery(id+"F49.opExtrude","CAP_FACE",FACE,{"disambiguationData":[OSD([sQuery(id+"F48.wireOp",EDGE,"E135"),sQuery(id+"F48.wireOp",EDGE,"E136"),sQuery(id+"F48.wireOp",EDGE,"E138.MirrorCS"),sQuery(id+"F48.wireOp",EDGE,"E141.MirrorCS")])],"isStart":false});
            var Q1;
            Q1=makeQuery(id+"F56.opExtrude","CAP_FACE",FACE,{"disambiguationData":[OSD([sQuery(id+"F55.wireOp",EDGE,"E148"),sQuery(id+"F55.wireOp",EDGE,"E149"),sQuery(id+"F55.wireOp",EDGE,"E150.MirrorCS"),sQuery(id+"F55.wireOp",EDGE,"E151.MirrorCS")])],"isStart":false});
            var Q2;
            Q2=makeQuery(id+"F49.opExtrude","CAP_FACE",FACE,{"disambiguationData":[OSD([sQuery(id+"F47.wireOp",EDGE,"E131"),sQuery(id+"F47.wireOp",EDGE,"E132"),sQuery(id+"F47.wireOp",EDGE,"E133.MirrorCS"),sQuery(id+"F47.wireOp",EDGE,"E134.MirrorCS")])],"isStart":false});
            var Q3;
            Q3=makeQuery(id+"F49.opExtrude","CAP_FACE",FACE,{"disambiguationData":[OSD([sQuery(id+"F46.wireOp",EDGE,"E127"),sQuery(id+"F46.wireOp",EDGE,"E128"),sQuery(id+"F46.wireOp",EDGE,"E129.MirrorCS"),sQuery(id+"F46.wireOp",EDGE,"E130.MirrorCS")])],"isStart":false});
            var Q4;
            {var subQ0=sQuery(id+"F45.wireOp",EDGE,"E124");Q4=makeQuery(id+"F45.imprint","IMPRINT",FACE,{"disambiguationData":[TD([[makeQuery(id+"F45.imprint","IMPRINT",EDGE,{"derivedFrom":subQ0}),1.0]])]});}
            loft(context, id + "F57", {"sheetProfilesArray" : [{ "sheetProfileEntities" : qUnion([Q0]) }, { "sheetProfileEntities" : qUnion([Q1]) }, { "sheetProfileEntities" : qUnion([Q2]) }, { "sheetProfileEntities" : qUnion([Q3]) }, { "sheetProfileEntities" : qUnion([Q4]) }]});
        }
        {
            var Q0;
            Q0=qCreatedBy(makeId("Right.planeOp"),FACE);
            var sketch = newSketch(context, id + "F58", { "sketchPlane" : qUnion([Q0])});
            skFitSpline(sketch, "E152", {"points": [v(76.9, 36.86) * mm, v(77.9, 37.13) * mm, v(81.38, 36.88) * mm, v(77.87, 36.58) * mm, v(76.9, 36.86) * mm]});
            skSolve(sketch);
        }
        {
            var Q0;
            Q0 = qSketchRegion(id + "F58", true);
            extrude(context, id + "F59", {"entities" : qUnion([Q0]), "operationType" : NewBodyOperationType.ADD, "oppositeDirection" : true, "depth" : 16.8 * mm, "offsetDistance" : 25.4 * mm});
        }
        {
            var Q0;
            Q0=qCreatedBy(makeId("Front.planeOp"),FACE);
            cPlane(context, id + "F60", {"entities" : qUnion([Q0]), "cplaneType" : CPlaneType.OFFSET, "offset" : 23.62 * mm, "width" : 152.4 * mm, "height" : 152.4 * mm});
        }
        {
            var Q0;
            Q0=qCreatedBy(id+"F60.planeOp",FACE);
            var sketch = newSketch(context, id + "F61", { "sketchPlane" : qUnion([Q0])});
            skLineSegment(sketch, "E153.bottom", {"start": v(-7.8, 21.02) * mm, "end": v(0.1, 21.02) * mm});
            skLineSegment(sketch, "E153.top", {"start": v(-7.8, 5.17) * mm, "end": v(0.1, 5.17) * mm});
            skLineSegment(sketch, "E153.left", {"start": v(-7.8, 21.02) * mm, "end": v(-7.8, 5.17) * mm});
            skLineSegment(sketch, "E153.right", {"start": v(0.1, 21.02) * mm, "end": v(0.1, 5.17) * mm});
            skLineSegment(sketch, "E154.MirrorCS", {"start": v(7.8, 21.02) * mm, "end": v(-0.1, 21.02) * mm});
            skLineSegment(sketch, "E155.MirrorCS", {"start": v(7.8, 21.02) * mm, "end": v(7.8, 5.17) * mm});
            skLineSegment(sketch, "E156.MirrorCS", {"start": v(7.8, 5.17) * mm, "end": v(-0.1, 5.17) * mm});
            skLineSegment(sketch, "E157.MirrorCS", {"start": v(-0.1, 21.02) * mm, "end": v(-0.1, 5.17) * mm});
            skSolve(sketch);
        }
        {
            var Q0;
            Q0=qCreatedBy(makeId("Front.planeOp"),FACE);
            var sketch = newSketch(context, id + "F62", { "sketchPlane" : qUnion([Q0])});
            skLineSegment(sketch, "E158.bottom", {"start": v(-9, 21.02) * mm, "end": v(0.08, 21.02) * mm});
            skLineSegment(sketch, "E158.top", {"start": v(-9, 1.78) * mm, "end": v(0.08, 1.78) * mm});
            skLineSegment(sketch, "E158.left", {"start": v(-9, 21.02) * mm, "end": v(-9, 1.78) * mm});
            skLineSegment(sketch, "E158.right", {"start": v(0.08, 21.02) * mm, "end": v(0.08, 1.78) * mm});
            skLineSegment(sketch, "E159.MirrorCS", {"start": v(9, 21.02) * mm, "end": v(-0.08, 21.02) * mm});
            skLineSegment(sketch, "E160.MirrorCS", {"start": v(-0.08, 21.02) * mm, "end": v(-0.08, 1.78) * mm});
            skLineSegment(sketch, "E161.MirrorCS", {"start": v(9, 21.02) * mm, "end": v(9, 1.78) * mm});
            skLineSegment(sketch, "E162.MirrorCS", {"start": v(9, 1.78) * mm, "end": v(-0.08, 1.78) * mm});
            skSolve(sketch);
        }
        {
            var Q0;
            Q0=qCreatedBy(id+"F3.planeOp",FACE);
            var sketch = newSketch(context, id + "F63", { "sketchPlane" : qUnion([Q0])});
            skLineSegment(sketch, "E163.bottom", {"start": v(-10.12, 21) * mm, "end": v(0.07, 21) * mm});
            skLineSegment(sketch, "E163.top", {"start": v(-10.12, 1.74) * mm, "end": v(0.07, 1.74) * mm});
            skLineSegment(sketch, "E163.left", {"start": v(-10.12, 21) * mm, "end": v(-10.12, 1.74) * mm});
            skLineSegment(sketch, "E163.right", {"start": v(0.07, 21) * mm, "end": v(0.07, 1.74) * mm});
            skLineSegment(sketch, "E164.MirrorCS", {"start": v(10.12, 21) * mm, "end": v(-0.07, 21) * mm});
            skLineSegment(sketch, "E165.MirrorCS", {"start": v(10.12, 21) * mm, "end": v(10.12, 1.74) * mm});
            skLineSegment(sketch, "E166.MirrorCS", {"start": v(10.12, 1.74) * mm, "end": v(-0.07, 1.74) * mm});
            skLineSegment(sketch, "E167.MirrorCS", {"start": v(-0.07, 21) * mm, "end": v(-0.07, 1.74) * mm});
            skSolve(sketch);
        }
        {
            var Q0;
            Q0 = qSketchRegion(id + "F63", true);
            var Q1;
            Q1 = qSketchRegion(id + "F62", true);
            var Q2;
            Q2 = qSketchRegion(id + "F61", true);
            extrude(context, id + "F64", {"entities" : qUnion([Q0, Q1, Q2]), "depth" : 0.03 * mm, "offsetDistance" : 25.4 * mm});
        }
        {
            var Q0;
            Q0 = qSketchRegion(id + "F58", true);
            extrude(context, id + "F65", {"entities" : qUnion([Q0]), "operationType" : NewBodyOperationType.ADD, "depth" : 16.79 * mm, "offsetDistance" : 25.4 * mm});
        }
        {
            var Q0;
            Q0=makeQuery(id+"F17.opExtrude","CAP_EDGE",EDGE,{"disambiguationData":[OSD([sQuery(id+"F16.wireOp",EDGE,"E54.MirrorCS")])],"isStart":true});
            fillet(context, id + "F66", {"entities" : qUnion([Q0]), "radius" : 2.45 * mm, "tangentPropagation" : true, "allowEdgeOverflow" : false});
        }
        {
            var Q0;
            Q0=makeQuery(id+"F17.opExtrude","CAP_EDGE",EDGE,{"disambiguationData":[OSD([sQuery(id+"F16.wireOp",EDGE,"E51")])],"isStart":true});
            fillet(context, id + "F67", {"entities" : qUnion([Q0]), "radius" : 2.45 * mm, "tangentPropagation" : true, "allowEdgeOverflow" : false});
        }
        {
            var Q0;
            Q0=qCreatedBy(id+"F42.planeOp",FACE);
            var sketch = newSketch(context, id + "F68", { "sketchPlane" : qUnion([Q0])});
            skLineSegment(sketch, "E168", {"start": v(64.6, 1.76) * mm, "end": v(64.6, 1.53) * mm});
            skFitSpline(sketch, "E169", {"points": [v(64.6, 1.76) * mm, v(78.4, 3.47) * mm, v(87.22, 6.66) * mm, v(87.9, 7.05) * mm, v(87.7, 6.66) * mm, v(78.53, 3.1) * mm, v(64.6, 1.53) * mm], "startDerivative": vector(52.7, 4.31) * mm, "endDerivative": vector(-53.59, -2.85) * mm});
            skSolve(sketch);
        }
        {
            var Q0;
            Q0 = qSketchRegion(id + "F68", true);
            extrude(context, id + "F69", {"entities" : qUnion([Q0]), "depth" : 38.13 * mm, "offsetDistance" : 25.4 * mm});
        }
        {
            var Q0;
            Q0=makeQuery(id+"F2.opExtrude","CAP_FACE",FACE,{"disambiguationData":[OSD([sQuery(id+"F1.wireOp",EDGE,"E0"),sQuery(id+"F1.wireOp",EDGE,"E1"),sQuery(id+"F1.wireOp",EDGE,"E2"),sQuery(id+"F1.wireOp",EDGE,"E3"),sQuery(id+"F1.wireOp",EDGE,"E4"),sQuery(id+"F1.wireOp",EDGE,"E5"),sQuery(id+"F1.wireOp",EDGE,"E6"),sQuery(id+"F1.wireOp",EDGE,"E7.MirrorCS"),sQuery(id+"F1.wireOp",EDGE,"E8.MirrorCS"),sQuery(id+"F1.wireOp",EDGE,"E9.MirrorCS"),sQuery(id+"F1.wireOp",EDGE,"E10.MirrorCS"),sQuery(id+"F1.wireOp",EDGE,"E11.MirrorCS"),sQuery(id+"F1.wireOp",EDGE,"E12.MirrorCS"),sQuery(id+"F1.wireOp",EDGE,"E13.MirrorCS")])],"isStart":false});
            var sketch = newSketch(context, id + "F70", { "sketchPlane" : qUnion([Q0])});
            skFitSpline(sketch, "E170", {"points": [v(10.35, -22.6) * mm, v(10.45, -22.9) * mm, v(10.6, -22.6) * mm, v(13.98, -9.1) * mm, v(20.82, -1.01) * mm, v(24.9, 1.34) * mm, v(25.8, 2) * mm, v(26.07, 2.63) * mm, v(25.58, 2.21) * mm, v(24.95, 1.72) * mm, v(24.22, 1.3) * mm, v(23.4, 0.89) * mm, v(22.78, 0.53) * mm, v(20.72, -0.82) * mm, v(17.9, -2.85) * mm, v(15.59, -5.47) * mm, v(13.84, -8.62) * mm, v(12.45, -12.66) * mm, v(11.35, -17.28) * mm, v(10.5, -21.4) * mm, v(10.35, -22.6) * mm]});
            skFitSpline(sketch, "E171.MirrorC", {"points": [v(-10.35, -22.6) * mm, v(-10.45, -22.9) * mm, v(-10.6, -22.6) * mm, v(-13.98, -9.1) * mm, v(-20.82, -1.01) * mm, v(-24.9, 1.34) * mm, v(-25.8, 2) * mm, v(-26.07, 2.63) * mm, v(-25.58, 2.21) * mm, v(-24.95, 1.72) * mm, v(-24.22, 1.3) * mm, v(-23.4, 0.89) * mm, v(-22.78, 0.53) * mm, v(-20.72, -0.82) * mm, v(-17.9, -2.85) * mm, v(-15.59, -5.47) * mm, v(-13.84, -8.62) * mm, v(-12.45, -12.66) * mm, v(-11.35, -17.28) * mm, v(-10.5, -21.4) * mm, v(-10.35, -22.6) * mm]});
            skSolve(sketch);
        }
        {
            var Q0;
            Q0 = qSketchRegion(id + "F70", true);
            extrude(context, id + "F71", {"entities" : qUnion([Q0]), "operationType" : NewBodyOperationType.ADD, "depth" : 6.35 * mm, "offsetDistance" : 25.4 * mm});
        }
        {
            var Q0;
            Q0=makeQuery(id+"F2.opExtrude","CAP_FACE",FACE,{"disambiguationData":[OSD([sQuery(id+"F1.wireOp",EDGE,"E0"),sQuery(id+"F1.wireOp",EDGE,"E1"),sQuery(id+"F1.wireOp",EDGE,"E2"),sQuery(id+"F1.wireOp",EDGE,"E3"),sQuery(id+"F1.wireOp",EDGE,"E4"),sQuery(id+"F1.wireOp",EDGE,"E5"),sQuery(id+"F1.wireOp",EDGE,"E6"),sQuery(id+"F1.wireOp",EDGE,"E7.MirrorCS"),sQuery(id+"F1.wireOp",EDGE,"E8.MirrorCS"),sQuery(id+"F1.wireOp",EDGE,"E9.MirrorCS"),sQuery(id+"F1.wireOp",EDGE,"E10.MirrorCS"),sQuery(id+"F1.wireOp",EDGE,"E11.MirrorCS"),sQuery(id+"F1.wireOp",EDGE,"E12.MirrorCS"),sQuery(id+"F1.wireOp",EDGE,"E13.MirrorCS")])],"isStart":false});
            var sketch = newSketch(context, id + "F72", { "sketchPlane" : qUnion([Q0])});
            skFitSpline(sketch, "E172", {"points": [v(28.6, 0.3) * mm, v(28.94, 0.68) * mm, v(29.86, 1.45) * mm, v(31.19, 3.4) * mm, v(31.7, 4.88) * mm, v(31.85, 5.37) * mm, v(31.8, 4.64) * mm, v(31.47, 3.42) * mm, v(30.04, 1.33) * mm, v(28.6, 0.3) * mm]});
            skFitSpline(sketch, "E173.MirrorC", {"points": [v(-28.6, 0.3) * mm, v(-28.94, 0.68) * mm, v(-29.86, 1.45) * mm, v(-31.19, 3.4) * mm, v(-31.7, 4.88) * mm, v(-31.85, 5.37) * mm, v(-31.8, 4.64) * mm, v(-31.47, 3.42) * mm, v(-30.04, 1.33) * mm, v(-28.6, 0.3) * mm]});
            skSolve(sketch);
        }
        {
            var Q0;
            Q0 = qSketchRegion(id + "F72", true);
            extrude(context, id + "F73", {"entities" : qUnion([Q0]), "operationType" : NewBodyOperationType.ADD, "depth" : 19.8 * mm, "offsetDistance" : 25.4 * mm});
        }
        {
            var Q0;
            Q0=qCreatedBy(makeId("Front.planeOp"),FACE);
            cPlane(context, id + "F74", {"entities" : qUnion([Q0]), "cplaneType" : CPlaneType.OFFSET, "offset" : 44.2 * mm, "width" : 152.4 * mm, "height" : 152.4 * mm});
        }
        {
            var Q0;
            Q0=qCreatedBy(id+"F74.planeOp",FACE);
            var sketch = newSketch(context, id + "F75", { "sketchPlane" : qUnion([Q0])});
            skLineSegment(sketch, "E174.bottom", {"start": v(-6.45, 20.63) * mm, "end": v(6.4, 20.63) * mm});
            skLineSegment(sketch, "E174.top", {"start": v(-6.45, 7.8) * mm, "end": v(6.4, 7.8) * mm});
            skLineSegment(sketch, "E174.left", {"start": v(-6.45, 20.63) * mm, "end": v(-6.45, 7.8) * mm});
            skLineSegment(sketch, "E174.right", {"start": v(6.4, 20.63) * mm, "end": v(6.4, 7.8) * mm});
            skSolve(sketch);
        }
        {
            var Q0;
            Q0=qCreatedBy(makeId("Front.planeOp"),FACE);
            cPlane(context, id + "F76", {"entities" : qUnion([Q0]), "cplaneType" : CPlaneType.OFFSET, "offset" : 84.07 * mm, "width" : 152.4 * mm, "height" : 152.4 * mm});
        }
        {
            var Q0;
            Q0=qCreatedBy(id+"F76.planeOp",FACE);
            var sketch = newSketch(context, id + "F77", { "sketchPlane" : qUnion([Q0])});
            skLineSegment(sketch, "E175.bottom", {"start": v(-5.85, 10.41) * mm, "end": v(5.67, 10.41) * mm});
            skLineSegment(sketch, "E175.top", {"start": v(-5.85, 7.02) * mm, "end": v(5.67, 7.02) * mm});
            skLineSegment(sketch, "E175.left", {"start": v(-5.85, 10.41) * mm, "end": v(-5.85, 7.02) * mm});
            skLineSegment(sketch, "E175.right", {"start": v(5.67, 10.41) * mm, "end": v(5.67, 7.02) * mm});
            skSolve(sketch);
        }
        {
            var Q0;
            Q0=makeQuery(id+"F64.opExtrude","CAP_FACE",FACE,{"disambiguationData":[OSD([sQuery(id+"F63.wireOp",EDGE,"E163.bottom"),sQuery(id+"F63.wireOp",EDGE,"E163.top"),sQuery(id+"F63.wireOp",EDGE,"E163.left"),sQuery(id+"F63.wireOp",EDGE,"E164.MirrorCS"),sQuery(id+"F63.wireOp",EDGE,"E165.MirrorCS"),sQuery(id+"F63.wireOp",EDGE,"E166.MirrorCS")])],"isStart":false});
            var Q1;
            Q1=makeQuery(id+"F64.opExtrude","CAP_FACE",FACE,{"disambiguationData":[OSD([sQuery(id+"F62.wireOp",EDGE,"E158.bottom"),sQuery(id+"F62.wireOp",EDGE,"E158.top"),sQuery(id+"F62.wireOp",EDGE,"E158.left"),sQuery(id+"F62.wireOp",EDGE,"E159.MirrorCS"),sQuery(id+"F62.wireOp",EDGE,"E161.MirrorCS"),sQuery(id+"F62.wireOp",EDGE,"E162.MirrorCS")])],"isStart":false});
            var Q2;
            Q2=makeQuery(id+"F64.opExtrude","CAP_FACE",FACE,{"disambiguationData":[OSD([sQuery(id+"F61.wireOp",EDGE,"E153.bottom"),sQuery(id+"F61.wireOp",EDGE,"E153.top"),sQuery(id+"F61.wireOp",EDGE,"E153.left"),sQuery(id+"F61.wireOp",EDGE,"E154.MirrorCS"),sQuery(id+"F61.wireOp",EDGE,"E155.MirrorCS"),sQuery(id+"F61.wireOp",EDGE,"E156.MirrorCS")])],"isStart":false});
            var Q3;
            Q3=makeQuery(id+"F75.imprint","IMPRINT",FACE,{"disambiguationData":[TD([[makeQuery(id+"F75.imprint","IMPRINT",EDGE,{"derivedFrom":sQuery(id+"F75.wireOp",EDGE,"E174.bottom")}),-1.0]])]});
            var Q4;
            Q4=makeQuery(id+"F77.imprint","IMPRINT",FACE,{"disambiguationData":[TD([[makeQuery(id+"F77.imprint","IMPRINT",EDGE,{"derivedFrom":sQuery(id+"F77.wireOp",EDGE,"E175.bottom")}),-1.0]])]});
            var Q5;
            Q5=makeQuery(id+"FNjUmohkJ9vkpSh_37.imprint","IMPRINT",FACE,{"disambiguationData":[TD([[makeQuery(id+"FNjUmohkJ9vkpSh_37.imprint","IMPRINT",EDGE,{"derivedFrom":sQuery(id+"FNjUmohkJ9vkpSh_37.wireOp",EDGE,"hFE55dvV-JmHA-kHDG-0T7m-Gz8EDarnrvbM.bottom")}),-1.0]])]});
            extrude(context, id + "F78", {"entities" : qUnion([Q0, Q1, Q2, Q3, Q4, Q5]), "depth" : 0.03 * mm, "offsetDistance" : 25.4 * mm});
        }
        {
            var Q0;
            Q0=qCreatedBy(id+"F42.planeOp",FACE);
            var sketch = newSketch(context, id + "F79", { "sketchPlane" : qUnion([Q0])});
            skCircle(sketch, "E176", {"center": v(-56.08, 10.82) * mm, "radius": 11.85 * mm});
            skSolve(sketch);
        }
        {
            var Q0;
            Q0 = qSketchRegion(id + "F79", true);
            extrude(context, id + "F80", {"entities" : qUnion([Q0]), "oppositeDirection" : true, "depth" : 16.26 * mm, "offsetDistance" : 25.4 * mm});
        }
        {
            var Q0;
            Q0=qCreatedBy(id+"F19.planeOp",FACE);
            var sketch = newSketch(context, id + "F81", { "sketchPlane" : qUnion([Q0])});
            skCircle(sketch, "E177", {"center": v(-56.15, 10.92) * mm, "radius": 11.85 * mm});
            skSolve(sketch);
        }
        {
            var Q0;
            Q0 = qSketchRegion(id + "F81", true);
            extrude(context, id + "F82", {"entities" : qUnion([Q0]), "depth" : 16.26 * mm, "offsetDistance" : 25.4 * mm});
        }
        {
            var Q0;
            Q0=makeQuery(id+"F82.opExtrude","CAP_EDGE",EDGE,{"disambiguationData":[OSD([sQuery(id+"F81.wireOp",EDGE,"E177")])],"isStart":false});
            fillet(context, id + "F83", {"entities" : qUnion([Q0]), "radius" : 1.29 * mm, "tangentPropagation" : true, "allowEdgeOverflow" : false});
        }
        {
            var Q0;
            Q0=makeQuery(id+"F82.opExtrude","CAP_EDGE",EDGE,{"disambiguationData":[OSD([sQuery(id+"F81.wireOp",EDGE,"E177")])],"isStart":true});
            fillet(context, id + "F84", {"entities" : qUnion([Q0]), "radius" : 1.29 * mm, "tangentPropagation" : true, "allowEdgeOverflow" : false});
        }
        {
            var Q0;
            Q0=makeQuery(id+"F80.opExtrude","CAP_EDGE",EDGE,{"disambiguationData":[OSD([sQuery(id+"F79.wireOp",EDGE,"E176")])],"isStart":false});
            var Q1;
            Q1=makeQuery(id+"F80.opExtrude","CAP_EDGE",EDGE,{"disambiguationData":[OSD([sQuery(id+"F79.wireOp",EDGE,"E176")])],"isStart":true});
            fillet(context, id + "F85", {"entities" : qUnion([Q0, Q1]), "radius" : 1.29 * mm, "tangentPropagation" : true, "allowEdgeOverflow" : false});
        }
        {
            var Q0;
            Q0=makeQuery(id+"F2.opExtrude","CAP_FACE",FACE,{"disambiguationData":[OSD([sQuery(id+"F1.wireOp",EDGE,"E0"),sQuery(id+"F1.wireOp",EDGE,"E1"),sQuery(id+"F1.wireOp",EDGE,"E2"),sQuery(id+"F1.wireOp",EDGE,"E3"),sQuery(id+"F1.wireOp",EDGE,"E4"),sQuery(id+"F1.wireOp",EDGE,"E5"),sQuery(id+"F1.wireOp",EDGE,"E6"),sQuery(id+"F1.wireOp",EDGE,"E7.MirrorCS"),sQuery(id+"F1.wireOp",EDGE,"E8.MirrorCS"),sQuery(id+"F1.wireOp",EDGE,"E9.MirrorCS"),sQuery(id+"F1.wireOp",EDGE,"E10.MirrorCS"),sQuery(id+"F1.wireOp",EDGE,"E11.MirrorCS"),sQuery(id+"F1.wireOp",EDGE,"E12.MirrorCS"),sQuery(id+"F1.wireOp",EDGE,"E13.MirrorCS")])],"isStart":true});
            var sketch = newSketch(context, id + "F86", { "sketchPlane" : qUnion([Q0])});
            skLineSegment(sketch, "E178", {"start": v(-34.15, 72.9) * mm, "end": v(-34.15, 87.22) * mm});
            skLineSegment(sketch, "E179", {"start": v(-34.15, 87.22) * mm, "end": v(0, 96.82) * mm});
            skLineSegment(sketch, "E180.MirrorCS", {"start": v(34.15, 72.9) * mm, "end": v(34.15, 87.22) * mm});
            skLineSegment(sketch, "E181.MirrorCS", {"start": v(34.15, 87.22) * mm, "end": v(0, 96.82) * mm});
            skFitSpline(sketch, "E182", {"points": [v(-34.15, 72.9) * mm, v(-22.36, 72.9) * mm, v(-21.07, 73.24) * mm, v(-19.85, 74.66) * mm, v(-16.53, 81.58) * mm, v(-5.07, 84.5) * mm, v(0.35, 84.7) * mm], "startDerivative": vector(61.38, -3.37) * mm, "endDerivative": vector(29.28, -0.5) * mm});
            skFitSpline(sketch, "E183.MirrorCS", {"points": [v(34.15, 72.9) * mm, v(22.36, 72.9) * mm, v(21.07, 73.24) * mm, v(19.85, 74.66) * mm, v(16.53, 81.58) * mm, v(5.07, 84.5) * mm, v(-0.35, 84.7) * mm], "startDerivative": vector(-61.38, -3.37) * mm, "endDerivative": vector(-29.28, -0.5) * mm});
            skSolve(sketch);
        }
        {
            var Q0;
            Q0=qCreatedBy(makeId("Front.planeOp"),FACE);
            cPlane(context, id + "F87", {"entities" : qUnion([Q0]), "cplaneType" : CPlaneType.OFFSET, "offset" : 71.37 * mm, "width" : 152.4 * mm, "height" : 152.4 * mm});
        }
        {
            var Q0;
            Q0=qCreatedBy(makeId("Front.planeOp"),FACE);
            cPlane(context, id + "F88", {"entities" : qUnion([Q0]), "cplaneType" : CPlaneType.OFFSET, "offset" : 77.72 * mm, "width" : 152.4 * mm, "height" : 152.4 * mm});
        }
        {
            var Q0;
            Q0=qCreatedBy(makeId("Front.planeOp"),FACE);
            cPlane(context, id + "F89", {"entities" : qUnion([Q0]), "cplaneType" : CPlaneType.OFFSET, "offset" : 89.92 * mm, "width" : 152.4 * mm, "height" : 152.4 * mm});
        }
        {
            var Q0;
            Q0=qCreatedBy(id+"F89.planeOp",FACE);
            var sketch = newSketch(context, id + "F90", { "sketchPlane" : qUnion([Q0])});
            skLineSegment(sketch, "E184", {"start": v(-6.12, 7) * mm, "end": v(-6.12, 8.34) * mm});
            skLineSegment(sketch, "E185", {"start": v(-6.12, 8.34) * mm, "end": v(0.22, 8.34) * mm});
            skLineSegment(sketch, "E186", {"start": v(-6.12, 7) * mm, "end": v(0.15, 7) * mm});
            skLineSegment(sketch, "E187", {"start": v(0.15, 7) * mm, "end": v(0.22, 8.34) * mm});
            skLineSegment(sketch, "E188.MirrorCS", {"start": v(6.12, 8.34) * mm, "end": v(-0.22, 8.34) * mm});
            skLineSegment(sketch, "E189.MirrorCS", {"start": v(-0.15, 7) * mm, "end": v(-0.22, 8.34) * mm});
            skLineSegment(sketch, "E190.MirrorCS", {"start": v(6.12, 7) * mm, "end": v(-0.15, 7) * mm});
            skLineSegment(sketch, "E191.MirrorCS", {"start": v(6.12, 7) * mm, "end": v(6.12, 8.34) * mm});
            skSolve(sketch);
        }
        {
            var Q0;
            Q0 = qSketchRegion(id + "F90", true);
            extrude(context, id + "F91", {"entities" : qUnion([Q0]), "depth" : 0.03 * mm, "offsetDistance" : 25.4 * mm});
        }
        {
            var Q0;
            Q0=qCreatedBy(id+"F87.planeOp",FACE);
            var sketch = newSketch(context, id + "F92", { "sketchPlane" : qUnion([Q0])});
            skLineSegment(sketch, "E192.bottom", {"start": v(-6.07, 15.02) * mm, "end": v(6, 15.02) * mm});
            skLineSegment(sketch, "E192.top", {"start": v(-6.07, 9.65) * mm, "end": v(6, 9.65) * mm});
            skLineSegment(sketch, "E192.left", {"start": v(-6.07, 15.02) * mm, "end": v(-6.07, 9.65) * mm});
            skLineSegment(sketch, "E192.right", {"start": v(6, 15.02) * mm, "end": v(6, 9.65) * mm});
            skSolve(sketch);
        }
        {
            var Q0;
            Q0 = qSketchRegion(id + "F92", true);
            extrude(context, id + "F93", {"entities" : qUnion([Q0]), "depth" : 0.03 * mm, "offsetDistance" : 25.4 * mm});
        }
        {
            var Q0;
            Q0=makeQuery(id+"F78.opExtrude","CAP_FACE",FACE,{"disambiguationData":[OSD([sQuery(id+"F63.wireOp",EDGE,"E163.bottom"),sQuery(id+"F63.wireOp",EDGE,"E163.top"),sQuery(id+"F63.wireOp",EDGE,"E163.left"),sQuery(id+"F63.wireOp",EDGE,"E164.MirrorCS"),sQuery(id+"F63.wireOp",EDGE,"E165.MirrorCS"),sQuery(id+"F63.wireOp",EDGE,"E166.MirrorCS")])],"isStart":false});
            var Q1;
            Q1=makeQuery(id+"F78.opExtrude","CAP_FACE",FACE,{"disambiguationData":[OSD([sQuery(id+"F62.wireOp",EDGE,"E158.bottom"),sQuery(id+"F62.wireOp",EDGE,"E158.top"),sQuery(id+"F62.wireOp",EDGE,"E158.left"),sQuery(id+"F62.wireOp",EDGE,"E159.MirrorCS"),sQuery(id+"F62.wireOp",EDGE,"E161.MirrorCS"),sQuery(id+"F62.wireOp",EDGE,"E162.MirrorCS")])],"isStart":false});
            var Q2;
            Q2=makeQuery(id+"F78.opExtrude","CAP_FACE",FACE,{"disambiguationData":[OSD([sQuery(id+"F61.wireOp",EDGE,"E153.bottom"),sQuery(id+"F61.wireOp",EDGE,"E153.top"),sQuery(id+"F61.wireOp",EDGE,"E153.left"),sQuery(id+"F61.wireOp",EDGE,"E154.MirrorCS"),sQuery(id+"F61.wireOp",EDGE,"E155.MirrorCS"),sQuery(id+"F61.wireOp",EDGE,"E156.MirrorCS")])],"isStart":false});
            var Q3;
            Q3=makeQuery(id+"F78.opExtrude","CAP_FACE",FACE,{"disambiguationData":[OSD([sQuery(id+"F75.wireOp",EDGE,"E174.bottom"),sQuery(id+"F75.wireOp",EDGE,"E174.top"),sQuery(id+"F75.wireOp",EDGE,"E174.left"),sQuery(id+"F75.wireOp",EDGE,"E174.right")])],"isStart":false});
            var Q4;
            Q4=makeQuery(id+"F93.opExtrude","CAP_FACE",FACE,{"disambiguationData":[OSD([sQuery(id+"F92.wireOp",EDGE,"E192.bottom"),sQuery(id+"F92.wireOp",EDGE,"E192.top"),sQuery(id+"F92.wireOp",EDGE,"E192.left"),sQuery(id+"F92.wireOp",EDGE,"E192.right")])],"isStart":false});
            var Q5;
            Q5=makeQuery(id+"F78.opExtrude","CAP_FACE",FACE,{"disambiguationData":[OSD([sQuery(id+"F77.wireOp",EDGE,"E175.bottom"),sQuery(id+"F77.wireOp",EDGE,"E175.top"),sQuery(id+"F77.wireOp",EDGE,"E175.left"),sQuery(id+"F77.wireOp",EDGE,"E175.right")])],"isStart":false});
            var Q6;
            Q6=makeQuery(id+"F91.opExtrude","CAP_FACE",FACE,{"disambiguationData":[OSD([sQuery(id+"F90.wireOp",EDGE,"E184"),sQuery(id+"F90.wireOp",EDGE,"E185"),sQuery(id+"F90.wireOp",EDGE,"E186"),sQuery(id+"F90.wireOp",EDGE,"E188.MirrorCS"),sQuery(id+"F90.wireOp",EDGE,"E190.MirrorCS"),sQuery(id+"F90.wireOp",EDGE,"E191.MirrorCS")])],"isStart":false});
            loft(context, id + "F94", {"sheetProfilesArray" : [{ "sheetProfileEntities" : qUnion([Q0]) }, { "sheetProfileEntities" : qUnion([Q1]) }, { "sheetProfileEntities" : qUnion([Q2]) }, { "sheetProfileEntities" : qUnion([Q3]) }, { "sheetProfileEntities" : qUnion([Q4]) }, { "sheetProfileEntities" : qUnion([Q5]) }, { "sheetProfileEntities" : qUnion([Q6]) }]});
        }
        {
            var Q0;
            Q0 = qSketchRegion(id + "F86", true);
            extrude(context, id + "F95", {"entities" : qUnion([Q0]), "depth" : 0.25 * mm, "offsetDistance" : 25.4 * mm});
        }
        {
            var Q0;
            Q0=makeQuery(id+"F95.opExtrude","CAP_FACE",FACE,{"disambiguationData":[OSD([sQuery(id+"F86.wireOp",EDGE,"E178"),sQuery(id+"F86.wireOp",EDGE,"E179"),sQuery(id+"F86.wireOp",EDGE,"E180.MirrorCS"),sQuery(id+"F86.wireOp",EDGE,"E181.MirrorCS"),sQuery(id+"F86.wireOp",EDGE,"E182"),sQuery(id+"F86.wireOp",EDGE,"E183.MirrorCS")])],"isStart":true});
            var sketch = newSketch(context, id + "F96", { "sketchPlane" : qUnion([Q0])});
            skFitSpline(sketch, "E193", {"points": [v(32.38, -87.72) * mm, v(32.63, -79.17) * mm, v(33.09, -77) * mm, v(34.15, -75.7) * mm], "startDerivative": vector(0.72, 20.33) * mm, "endDerivative": vector(8.3, 5.26) * mm});
            skFitSpline(sketch, "E194", {"points": [v(28.24, -84.13) * mm, v(28.42, -80.54) * mm, v(28.99, -77.3) * mm, v(29.9, -74.56) * mm], "startDerivative": vector(0.24, 10.33) * mm, "endDerivative": vector(3.14, 8.5) * mm});
            skFitSpline(sketch, "E195", {"points": [v(25.34, -84.19) * mm, v(25.62, -80.2) * mm, v(26.36, -76.72) * mm, v(27.22, -74.39) * mm], "startDerivative": vector(0.46, 10.98) * mm, "endDerivative": vector(3.08, 7.66) * mm});
            skFitSpline(sketch, "E196", {"points": [v(20.72, -84.13) * mm, v(21.35, -79.57) * mm, v(21.95, -76.38) * mm, v(22.48, -74.36) * mm], "startDerivative": vector(1.4, 11.36) * mm, "endDerivative": vector(1.04, 5.86) * mm});
            skFitSpline(sketch, "E197.MirrorCS", {"points": [v(-20.72, -84.13) * mm, v(-21.35, -79.57) * mm, v(-21.95, -76.38) * mm, v(-22.48, -74.36) * mm], "startDerivative": vector(-1.4, 11.36) * mm, "endDerivative": vector(-1.04, 5.86) * mm});
            skFitSpline(sketch, "E198.MirrorCS", {"points": [v(-25.34, -84.19) * mm, v(-25.62, -80.2) * mm, v(-26.36, -76.72) * mm, v(-27.22, -74.39) * mm], "startDerivative": vector(-0.46, 10.98) * mm, "endDerivative": vector(-3.08, 7.66) * mm});
            skFitSpline(sketch, "E199.MirrorCS", {"points": [v(-28.24, -84.13) * mm, v(-28.42, -80.54) * mm, v(-28.99, -77.3) * mm, v(-29.9, -74.56) * mm], "startDerivative": vector(-0.24, 10.33) * mm, "endDerivative": vector(-3.14, 8.5) * mm});
            skFitSpline(sketch, "E200.MirrorCS", {"points": [v(-32.38, -87.72) * mm, v(-32.63, -79.17) * mm, v(-33.09, -77) * mm, v(-34.15, -75.7) * mm], "startDerivative": vector(-0.72, 20.33) * mm, "endDerivative": vector(-8.3, 5.26) * mm});
            skFitSpline(sketch, "E201", {"points": [v(22.48, -74.36) * mm, v(22.61, -74.36) * mm, v(22.18, -76.47) * mm, v(21.55, -79.62) * mm, v(21.1, -82.62) * mm, v(20.83, -84.17) * mm, v(20.72, -84.4) * mm, v(20.72, -84.13) * mm], "startDerivative": vector(4.44, 1.37) * mm, "endDerivative": vector(0.72, 5.57) * mm});
            skFitSpline(sketch, "E202", {"points": [v(27.22, -74.39) * mm, v(27.22, -74.75) * mm, v(26.86, -75.74) * mm, v(26.52, -76.79) * mm, v(26.01, -79.03) * mm, v(25.75, -81.13) * mm, v(25.57, -84.08) * mm, v(25.52, -84.25) * mm, v(25.42, -84.36) * mm, v(25.34, -84.19) * mm], "startDerivative": vector(0.6, -4.48) * mm, "endDerivative": vector(-1.48, 4.97) * mm});
            skFitSpline(sketch, "E203", {"points": [v(29.9, -74.56) * mm, v(29.9, -74.84) * mm, v(29.49, -76.2) * mm, v(29.05, -77.87) * mm, v(28.72, -79.6) * mm, v(28.53, -81.64) * mm, v(28.45, -83.54) * mm, v(28.46, -84.06) * mm, v(28.43, -84.18) * mm, v(28.33, -84.3) * mm, v(28.28, -84.27) * mm, v(28.24, -84.13) * mm], "startDerivative": vector(0.53, -4.01) * mm, "endDerivative": vector(-0.58, 3.91) * mm});
            skFitSpline(sketch, "E204", {"points": [v(32.38, -87.72) * mm, v(32.27, -87.58) * mm, v(32.26, -87.26) * mm, v(32.47, -79.2) * mm, v(32.77, -77.37) * mm, v(33.2, -76.38) * mm, v(33.82, -75.8) * mm, v(34.15, -75.7) * mm], "startDerivative": vector(-2.4, 2.64) * mm, "endDerivative": vector(4.14, 0.6) * mm});
            skFitSpline(sketch, "E205.MirrorCS", {"points": [v(-22.48, -74.36) * mm, v(-22.61, -74.36) * mm, v(-22.18, -76.47) * mm, v(-21.55, -79.62) * mm, v(-21.1, -82.62) * mm, v(-20.83, -84.17) * mm, v(-20.72, -84.4) * mm, v(-20.72, -84.13) * mm], "startDerivative": vector(-4.44, 1.37) * mm, "endDerivative": vector(-0.72, 5.57) * mm});
            skFitSpline(sketch, "E206.MirrorCS", {"points": [v(-27.22, -74.39) * mm, v(-27.22, -74.75) * mm, v(-26.86, -75.74) * mm, v(-26.52, -76.79) * mm, v(-26.01, -79.03) * mm, v(-25.75, -81.13) * mm, v(-25.57, -84.08) * mm, v(-25.52, -84.25) * mm, v(-25.42, -84.36) * mm, v(-25.34, -84.19) * mm], "startDerivative": vector(-0.6, -4.48) * mm, "endDerivative": vector(1.48, 4.97) * mm});
            skFitSpline(sketch, "E207.MirrorCS", {"points": [v(-29.9, -74.56) * mm, v(-29.9, -74.84) * mm, v(-29.49, -76.2) * mm, v(-29.05, -77.87) * mm, v(-28.72, -79.6) * mm, v(-28.53, -81.64) * mm, v(-28.45, -83.54) * mm, v(-28.46, -84.06) * mm, v(-28.43, -84.18) * mm, v(-28.33, -84.3) * mm, v(-28.28, -84.27) * mm, v(-28.24, -84.13) * mm], "startDerivative": vector(-0.53, -4.01) * mm, "endDerivative": vector(0.58, 3.91) * mm});
            skFitSpline(sketch, "E208.MirrorCS", {"points": [v(-32.38, -87.72) * mm, v(-32.27, -87.58) * mm, v(-32.26, -87.26) * mm, v(-32.47, -79.2) * mm, v(-32.77, -77.37) * mm, v(-33.2, -76.38) * mm, v(-33.82, -75.8) * mm, v(-34.15, -75.7) * mm], "startDerivative": vector(2.4, 2.64) * mm, "endDerivative": vector(-4.14, 0.6) * mm});
            skSolve(sketch);
        }
        {
            var Q0;
            Q0 = qSketchRegion(id + "F96", true);
            extrude(context, id + "F97", {"entities" : qUnion([Q0]), "operationType" : NewBodyOperationType.ADD, "depth" : 6.6 * mm, "offsetDistance" : 25.4 * mm});
        }
        {
            var Q0;
            Q0=makeQuery(id+"F94.opLoft","MID_CAP_EDGE",EDGE,{"disambiguationData":[OSD([sQuery(id+"F90.wireOp",EDGE,"E184"),sQuery(id+"F90.wireOp",EDGE,"E185"),sQuery(id+"F90.wireOp",EDGE,"E188.MirrorCS"),sQuery(id+"F90.wireOp",EDGE,"E191.MirrorCS")])],"capPos":6.0});
            var Q1;
            Q1=makeQuery(id+"F94.opLoft","MID_CAP_EDGE",EDGE,{"disambiguationData":[OSD([sQuery(id+"F90.wireOp",EDGE,"E184"),sQuery(id+"F90.wireOp",EDGE,"E186"),sQuery(id+"F90.wireOp",EDGE,"E190.MirrorCS"),sQuery(id+"F90.wireOp",EDGE,"E191.MirrorCS")])],"capPos":6.0});
            fillet(context, id + "F98", {"entities" : qUnion([Q0, Q1]), "radius" : 0.59 * mm, "tangentPropagation" : true, "allowEdgeOverflow" : false});
        }
        {
            var Q0;
            Q0=qCreatedBy(id+"F5.planeOp",FACE);
            var sketch = newSketch(context, id + "F99", { "sketchPlane" : qUnion([Q0])});
            skFitSpline(sketch, "E209", {"points": [v(-13.39, 20.1) * mm, v(-12.43, 23.64) * mm, v(-6.63, 23.38) * mm, v(-5.9, 22.14) * mm, v(-3.2, 21.7) * mm, v(0.34, 17.54) * mm], "startDerivative": vector(-2.73, 15.44) * mm, "endDerivative": vector(-152.13, -55.17) * mm});
            skLineSegment(sketch, "E210", {"start": v(0.23, 17.54) * mm, "end": v(0.34, 17.54) * mm});
            skLineSegment(sketch, "E211", {"start": v(-13.39, 20.1) * mm, "end": v(0.23, 17.54) * mm});
            skFitSpline(sketch, "E212.MirrorCS", {"points": [v(13.39, 20.1) * mm, v(12.43, 23.64) * mm, v(6.63, 23.38) * mm, v(5.9, 22.14) * mm, v(3.2, 21.7) * mm, v(-0.34, 17.54) * mm], "startDerivative": vector(2.73, 15.44) * mm, "endDerivative": vector(152.13, -55.17) * mm});
            skLineSegment(sketch, "E213.MirrorCS", {"start": v(-0.23, 17.54) * mm, "end": v(-0.34, 17.54) * mm});
            skLineSegment(sketch, "E214.MirrorCS", {"start": v(13.39, 20.1) * mm, "end": v(-0.23, 17.54) * mm});
            skSolve(sketch);
        }
        {
            var Q0;
            Q0=makeQuery(id+"F71.opExtrude","CAP_FACE",FACE,{"disambiguationData":[OSD([sQuery(id+"F70.wireOp",EDGE,"E170")])],"isStart":false});
            var sketch = newSketch(context, id + "F100", { "sketchPlane" : qUnion([Q0])});
            skFitSpline(sketch, "E215", {"points": [v(10.44, -22.88) * mm, v(10.34, -22.54) * mm, v(10.4, -21.9) * mm, v(12.25, -13.39) * mm, v(13.86, -8.84) * mm, v(17.82, -4.27) * mm, v(22.65, -2.44) * mm, v(24.3, -1.73) * mm, v(24.35, -1.8) * mm, v(24.17, -1.95) * mm, v(22.7, -2.67) * mm, v(19.87, -3.58) * mm, v(17.98, -4.45) * mm, v(16.27, -5.8) * mm, v(14.24, -8.72) * mm, v(13.56, -10.16) * mm, v(12.48, -13.62) * mm, v(11.32, -18.8) * mm, v(10.64, -22.4) * mm, v(10.56, -22.72) * mm, v(10.44, -22.88) * mm]});
            skFitSpline(sketch, "E216.MirrorC", {"points": [v(-10.44, -22.88) * mm, v(-10.34, -22.54) * mm, v(-10.4, -21.9) * mm, v(-12.25, -13.39) * mm, v(-13.86, -8.84) * mm, v(-17.82, -4.27) * mm, v(-22.65, -2.44) * mm, v(-24.3, -1.73) * mm, v(-24.35, -1.8) * mm, v(-24.17, -1.95) * mm, v(-22.7, -2.67) * mm, v(-19.87, -3.58) * mm, v(-17.98, -4.45) * mm, v(-16.27, -5.8) * mm, v(-14.24, -8.72) * mm, v(-13.56, -10.16) * mm, v(-12.48, -13.62) * mm, v(-11.32, -18.8) * mm, v(-10.64, -22.4) * mm, v(-10.56, -22.72) * mm, v(-10.44, -22.88) * mm]});
            skSolve(sketch);
        }
        {
            var Q0;
            Q0 = qSketchRegion(id + "F100", true);
            extrude(context, id + "F101", {"entities" : qUnion([Q0]), "operationType" : NewBodyOperationType.ADD, "depth" : 4.57 * mm, "offsetDistance" : 25.4 * mm});
        }
        {
            var Q0;
            Q0=makeQuery(id+"F101.opExtrude","CAP_FACE",FACE,{"disambiguationData":[OSD([sQuery(id+"F100.wireOp",EDGE,"E215")])],"isStart":false});
            var sketch = newSketch(context, id + "F102", { "sketchPlane" : qUnion([Q0])});
            skFitSpline(sketch, "E217", {"points": [v(18.46, -5.17) * mm, v(18.41, -5) * mm, v(18.5, -4.72) * mm, v(18.75, -4.24) * mm, v(19.07, -3.9) * mm, v(19.98, -3.3) * mm, v(22.6, -2.46) * mm, v(23.83, -2.14) * mm, v(25.03, -1.81) * mm, v(25.57, -1.6) * mm, v(25.42, -1.87) * mm, v(25.15, -2.04) * mm, v(24.55, -2.22) * mm, v(23.72, -2.4) * mm, v(22.05, -2.9) * mm, v(21.49, -3.09) * mm, v(20.4, -3.4) * mm, v(19.79, -3.61) * mm, v(19.06, -4.18) * mm, v(18.68, -4.77) * mm, v(18.57, -5.05) * mm, v(18.46, -5.17) * mm]});
            skFitSpline(sketch, "E218.MirrorC", {"points": [v(-18.46, -5.17) * mm, v(-18.41, -5) * mm, v(-18.5, -4.72) * mm, v(-18.75, -4.24) * mm, v(-19.07, -3.9) * mm, v(-19.98, -3.3) * mm, v(-22.6, -2.46) * mm, v(-23.83, -2.14) * mm, v(-25.03, -1.81) * mm, v(-25.57, -1.6) * mm, v(-25.42, -1.87) * mm, v(-25.15, -2.04) * mm, v(-24.55, -2.22) * mm, v(-23.72, -2.4) * mm, v(-22.05, -2.9) * mm, v(-21.49, -3.09) * mm, v(-20.4, -3.4) * mm, v(-19.79, -3.61) * mm, v(-19.06, -4.18) * mm, v(-18.68, -4.77) * mm, v(-18.57, -5.05) * mm, v(-18.46, -5.17) * mm]});
            skSolve(sketch);
        }
        {
            var Q0;
            Q0 = qSketchRegion(id + "F102", true);
            extrude(context, id + "F103", {"entities" : qUnion([Q0]), "operationType" : NewBodyOperationType.ADD, "depth" : 1.8 * mm, "offsetDistance" : 25.4 * mm});
        }
        {
            var Q0;
            Q0=qCreatedBy(id+"F20.planeOp",FACE);
            var sketch = newSketch(context, id + "F104", { "sketchPlane" : qUnion([Q0])});
            skFitSpline(sketch, "E219", {"points": [v(-14.97, 18.36) * mm, v(-16.1, 18.73) * mm, v(-21.04, 19.13) * mm, v(-22.77, 19.16) * mm, v(-23.2, 19.01) * mm, v(-22.17, 18.86) * mm, v(-20.94, 18.81) * mm, v(-19.47, 18.71) * mm, v(-16.34, 18.36) * mm, v(-15.42, 18.16) * mm, v(-14.55, 17.98) * mm, v(-14.97, 18.36) * mm]});
            skSolve(sketch);
        }
        {
            var Q0;
            Q0 = qSketchRegion(id + "F104", true);
            extrude(context, id + "F105", {"entities" : qUnion([Q0]), "operationType" : NewBodyOperationType.ADD, "depth" : 40.4 * mm, "offsetDistance" : 25.4 * mm});
        }
        {
            var Q0;
            Q0=qCreatedBy(id+"F76.planeOp",FACE);
            var sketch = newSketch(context, id + "F106", { "sketchPlane" : qUnion([Q0])});
            skFitSpline(sketch, "E220", {"points": [v(-7.01, 1.49) * mm, v(-6.08, 4.82) * mm, v(-6.03, 7.01) * mm, v(-5.97, 7.12) * mm, v(-5.89, 7.15) * mm, v(-5.72, 7.12) * mm, v(-5.66, 6.98) * mm, v(-5.66, 5.75) * mm, v(-5.7, 4.85) * mm, v(-6, 3.14) * mm, v(-6.59, 1.49) * mm, v(-6.67, 1.37) * mm, v(-6.73, 1.35) * mm, v(-6.86, 1.31) * mm, v(-6.97, 1.3) * mm, v(-7.01, 1.34) * mm, v(-7.02, 1.4) * mm, v(-7.01, 1.44) * mm, v(-7.01, 1.49) * mm]});
            skFitSpline(sketch, "E221.MirrorC", {"points": [v(7.01, 1.49) * mm, v(6.08, 4.82) * mm, v(6.03, 7.01) * mm, v(5.97, 7.12) * mm, v(5.89, 7.15) * mm, v(5.72, 7.12) * mm, v(5.66, 6.98) * mm, v(5.66, 5.75) * mm, v(5.7, 4.85) * mm, v(6, 3.14) * mm, v(6.59, 1.49) * mm, v(6.67, 1.37) * mm, v(6.73, 1.35) * mm, v(6.86, 1.31) * mm, v(6.97, 1.3) * mm, v(7.01, 1.34) * mm, v(7.02, 1.4) * mm, v(7.01, 1.44) * mm, v(7.01, 1.49) * mm]});
            skSolve(sketch);
        }
        {
            var Q0;
            Q0 = qSketchRegion(id + "F106", true);
            extrude(context, id + "F107", {"entities" : qUnion([Q0]), "depth" : 1.45 * mm, "offsetDistance" : 25.4 * mm});
        }
        {
            var Q0;
            Q0=qCreatedBy(id+"F88.planeOp",FACE);
            var sketch = newSketch(context, id + "F108", { "sketchPlane" : qUnion([Q0])});
            skFitSpline(sketch, "E222", {"points": [v(5.92, 1.48) * mm, v(5.94, 1.46) * mm, v(5.97, 1.43) * mm, v(5.98, 1.4) * mm, v(5.93, 1.4) * mm, v(5.87, 1.4) * mm, v(5.8, 1.43) * mm, v(5.76, 1.47) * mm, v(5.72, 1.5) * mm, v(5.1, 3.17) * mm, v(4.68, 5.25) * mm, v(4.85, 7.21) * mm, v(5.04, 7.68) * mm, v(5.14, 7.85) * mm, v(5.41, 7.79) * mm, v(5.36, 7.59) * mm, v(4.84, 5.33) * mm, v(5.92, 1.48) * mm]});
            skFitSpline(sketch, "E223.MirrorC", {"points": [v(-5.92, 1.48) * mm, v(-5.94, 1.46) * mm, v(-5.97, 1.43) * mm, v(-5.98, 1.4) * mm, v(-5.93, 1.4) * mm, v(-5.87, 1.4) * mm, v(-5.8, 1.43) * mm, v(-5.76, 1.47) * mm, v(-5.72, 1.5) * mm, v(-5.1, 3.17) * mm, v(-4.68, 5.25) * mm, v(-4.85, 7.21) * mm, v(-5.04, 7.68) * mm, v(-5.14, 7.85) * mm, v(-5.41, 7.79) * mm, v(-5.36, 7.59) * mm, v(-4.84, 5.33) * mm, v(-5.92, 1.48) * mm]});
            skSolve(sketch);
        }
        {
            var Q0;
            Q0 = qSketchRegion(id + "F108", true);
            extrude(context, id + "F109", {"entities" : qUnion([Q0]), "operationType" : NewBodyOperationType.ADD, "oppositeDirection" : true, "depth" : 3 * mm, "offsetDistance" : 25.4 * mm});
        }
        {
            var Q0;
            Q0=makeQuery(id+"F106.imprint","IMPRINT",FACE,{"disambiguationData":[TD([[makeQuery(id+"F106.imprint","IMPRINT",EDGE,{"derivedFrom":sQuery(id+"F106.wireOp",EDGE,"E221.MirrorC")}),1.0]])]});
            var Q1;
            Q1=makeQuery(id+"F109.opExtrude","CAP_FACE",FACE,{"disambiguationData":[OSD([sQuery(id+"F108.wireOp",EDGE,"E222")])],"isStart":true});
            var Q2;
            Q2=makeQuery(id+"F109.opExtrude","CAP_FACE",FACE,{"disambiguationData":[OSD([sQuery(id+"F108.wireOp",EDGE,"E222")])],"isStart":false});
            loft(context, id + "F110", {"sheetProfilesArray" : [{ "sheetProfileEntities" : qUnion([Q0]) }, { "sheetProfileEntities" : qUnion([Q1]) }, { "sheetProfileEntities" : qUnion([Q2]) }]});
        }
        {
            var Q0;
            Q0=makeQuery(id+"F106.imprint","IMPRINT",FACE,{"disambiguationData":[TD([[makeQuery(id+"F106.imprint","IMPRINT",EDGE,{"derivedFrom":sQuery(id+"F106.wireOp",EDGE,"E220")}),-1.0]])]});
            var Q1;
            Q1=makeQuery(id+"F109.opExtrude","CAP_FACE",FACE,{"disambiguationData":[OSD([sQuery(id+"F108.wireOp",EDGE,"E223.MirrorC")])],"isStart":true});
            var Q2;
            Q2=makeQuery(id+"F109.opExtrude","CAP_FACE",FACE,{"disambiguationData":[OSD([sQuery(id+"F108.wireOp",EDGE,"E223.MirrorC")])],"isStart":false});
            loft(context, id + "F111", {"sheetProfilesArray" : [{ "sheetProfileEntities" : qUnion([Q0]) }, { "sheetProfileEntities" : qUnion([Q1]) }, { "sheetProfileEntities" : qUnion([Q2]) }]});
        }
        {
            var Q0;
            Q0=makeQuery(id+"F105.opExtrude","CAP_EDGE",EDGE,{"disambiguationData":[OSD([sQuery(id+"F104.wireOp",EDGE,"E219")])],"isStart":false});
            fillet(context, id + "F112", {"entities" : qUnion([Q0]), "radius" : 0.14 * mm, "tangentPropagation" : true, "allowEdgeOverflow" : false});
        }
        {
            var Q0;
            Q0=makeQuery(id+"F105.opExtrude","CAP_EDGE",EDGE,{"disambiguationData":[OSD([sQuery(id+"F104.wireOp",EDGE,"E219")])],"isStart":true});
            fillet(context, id + "F113", {"entities" : qUnion([Q0]), "radius" : 0.12 * mm, "tangentPropagation" : true, "allowEdgeOverflow" : false});
        }
        {
            var Q0;
            Q0=makeQuery(id+"F26.opExtrude","CAP_EDGE",EDGE,{"disambiguationData":[OSD([sQuery(id+"F25.wireOp",EDGE,"E70")])],"isStart":false});
            fillet(context, id + "F114", {"entities" : qUnion([Q0]), "radius" : 0.1 * mm, "tangentPropagation" : true, "allowEdgeOverflow" : false});
        }
        {
            var Q0;
            Q0=makeQuery(id+"F26.opExtrude","CAP_EDGE",EDGE,{"disambiguationData":[OSD([sQuery(id+"F25.wireOp",EDGE,"E73.MirrorCS")])],"isStart":false});
            fillet(context, id + "F115", {"entities" : qUnion([Q0]), "radius" : 0.1 * mm, "tangentPropagation" : true, "allowEdgeOverflow" : false});
        }
        {
            var Q0;
            Q0=makeQuery(id+"F49.opExtrude","CAP_FACE",FACE,{"disambiguationData":[OSD([sQuery(id+"F45.wireOp",EDGE,"E123"),sQuery(id+"F45.wireOp",EDGE,"E124"),sQuery(id+"F45.wireOp",EDGE,"E125.MirrorCS"),sQuery(id+"F45.wireOp",EDGE,"E126.MirrorCS")])],"isStart":false});
            var sketch = newSketch(context, id + "F116", { "sketchPlane" : qUnion([Q0])});
            skFitSpline(sketch, "E224", {"points": [v(-13.54, 20.97) * mm, v(-12.78, 23.31) * mm, v(-11.68, 24.05) * mm, v(-10, 24.3) * mm, v(-8.19, 24.4) * mm, v(7.93, 24.43) * mm, v(11.22, 24.16) * mm, v(12.32, 23.76) * mm, v(13.12, 22.7) * mm, v(13.57, 20.76) * mm], "startDerivative": vector(5.32, 25.68) * mm, "endDerivative": vector(3.64, -21.57) * mm});
            skLineSegment(sketch, "E225", {"start": v(-13.54, 20.97) * mm, "end": v(13.57, 20.76) * mm});
            skSolve(sketch);
        }
        {
            var Q0;
            Q0 = qSketchRegion(id + "F116", true);
            extrude(context, id + "F117", {"entities" : qUnion([Q0]), "depth" : 2.18 * mm, "offsetDistance" : 25.4 * mm});
        }
        {
            var Q0;
            Q0 = qSketchRegion(id + "F99", true);
            extrude(context, id + "F118", {"entities" : qUnion([Q0]), "oppositeDirection" : true, "depth" : 5.97 * mm, "offsetDistance" : 25.4 * mm});
        }
        {
            var Q0;
            {var subQ0=sQuery(id+"F99.wireOp",EDGE,"E212.MirrorCS");Q0=makeQuery(id+"F118.opExtrude","CAP_EDGE",EDGE,{"disambiguationData":[OSD([subQ0]),TDD([makeQuery(id+"F99.imprint","IMPRINT",EDGE,{"disambiguationData":[TD([[makeQuery(id+"F99.imprint","INTERSECT",VERTEX,{"derivedFrom":[subQ0,sQuery(id+"F99.wireOp",EDGE,"E214.MirrorCS")]}),-1.0]])],"derivedFrom":subQ0})])],"isStart":true});}
            var Q1;
            {var subQ0=sQuery(id+"F99.wireOp",EDGE,"E209");Q1=makeQuery(id+"F118.opExtrude","CAP_EDGE",EDGE,{"disambiguationData":[OSD([subQ0]),TDD([makeQuery(id+"F99.imprint","IMPRINT",EDGE,{"disambiguationData":[TD([[makeQuery(id+"F99.imprint","INTERSECT",VERTEX,{"derivedFrom":[subQ0,sQuery(id+"F99.wireOp",EDGE,"E211")]}),-1.0]])],"derivedFrom":subQ0})])],"isStart":true});}
            fillet(context, id + "F119", {"entities" : qUnion([Q0, Q1]), "radius" : 0.43 * mm, "tangentPropagation" : true, "allowEdgeOverflow" : false});
        }
        {
            var Q0;
            Q0=makeQuery(id+"F17.opExtrude","CAP_EDGE",EDGE,{"disambiguationData":[OSD([sQuery(id+"F4.wireOp",EDGE,"E15")])],"isStart":false});
            var Q1;
            Q1=makeQuery(id+"F17.opExtrude","CAP_EDGE",EDGE,{"disambiguationData":[OSD([sQuery(id+"F4.wireOp",EDGE,"E18.MirrorCS")])],"isStart":false});
            fillet(context, id + "F120", {"entities" : qUnion([Q0, Q1]), "radius" : 11.53 * mm, "tangentPropagation" : true, "allowEdgeOverflow" : false});
        }
        {
            var Q0;
            Q0=makeQuery(id+"F49.opExtrude","CAP_FACE",FACE,{"disambiguationData":[OSD([sQuery(id+"F45.wireOp",EDGE,"E123"),sQuery(id+"F45.wireOp",EDGE,"E124"),sQuery(id+"F45.wireOp",EDGE,"E125.MirrorCS"),sQuery(id+"F45.wireOp",EDGE,"E126.MirrorCS")])],"isStart":false});
            var sketch = newSketch(context, id + "F121", { "sketchPlane" : qUnion([Q0])});
            skFitSpline(sketch, "E226", {"points": [v(0, 37.13) * mm, v(-1.23, 36.96) * mm, v(-2.75, 36.3) * mm, v(-3.44, 35.25) * mm, v(-3.6, 34.11) * mm, v(-3.6, 33.26) * mm, v(-3.57, 33.18) * mm, v(-3.14, 32.98) * mm, v(-2.9, 32.88) * mm, v(-1.87, 32.56) * mm, v(-1.05, 32.38) * mm, v(-0.45, 32.3) * mm, v(0, 32.28) * mm], "startDerivative": vector(-11, -0.95) * mm, "endDerivative": vector(12.3, -0.58) * mm});
            skFitSpline(sketch, "E227.MirrorCS", {"points": [v(0, 37.13) * mm, v(1.23, 36.96) * mm, v(2.75, 36.3) * mm, v(3.44, 35.25) * mm, v(3.6, 34.11) * mm, v(3.6, 33.26) * mm, v(3.57, 33.18) * mm, v(3.14, 32.98) * mm, v(2.9, 32.88) * mm, v(1.87, 32.56) * mm, v(1.05, 32.38) * mm, v(0.45, 32.3) * mm, v(0, 32.28) * mm], "startDerivative": vector(11, -0.95) * mm, "endDerivative": vector(-12.3, -0.58) * mm});
            skSolve(sketch);
        }
        {
            var Q0;
            Q0 = qSketchRegion(id + "F121", true);
            extrude(context, id + "F122", {"entities" : qUnion([Q0]), "operationType" : NewBodyOperationType.ADD, "depth" : 3.73 * mm, "offsetDistance" : 25.4 * mm});
        }
        {
            var Q0;
            Q0=makeQuery(id+"F122.opExtrude","CAP_EDGE",EDGE,{"disambiguationData":[OSD([sQuery(id+"F121.wireOp",EDGE,"E226")])],"isStart":false});
            var Q1;
            Q1=makeQuery(id+"F122.opExtrude","CAP_EDGE",EDGE,{"disambiguationData":[OSD([sQuery(id+"F121.wireOp",EDGE,"E227.MirrorCS")])],"isStart":false});
            fillet(context, id + "F123", {"entities" : qUnion([Q0, Q1]), "radius" : 0.98 * mm, "tangentPropagation" : true, "allowEdgeOverflow" : false});
        }
        {
            var Q0;
            {var subQ0=sQuery(id+"F45.wireOp",EDGE,"E123");var subQ1=sQuery(id+"F45.wireOp",EDGE,"E126.MirrorCS");var subQ2=sQuery(id+"F45.wireOp",EDGE,"E124");Q0=makeQuery(id+"F122.boolean.opBoolean","SPLIT",EDGE,{"disambiguationData":[TD([makeQuery(id+"F49.opExtrude","SWEPT_FACE",FACE,{"disambiguationData":[OSD([subQ0])]}),makeQuery(id+"F49.opExtrude","CAP_FACE",FACE,{"disambiguationData":[OSD([subQ0,subQ2,sQuery(id+"F45.wireOp",EDGE,"E125.MirrorCS"),subQ1])],"isStart":false}),makeQuery(id+"F49.opExtrude","SWEPT_FACE",FACE,{"disambiguationData":[OSD([subQ2,subQ1])]}),makeQuery(id+"F122.opExtrude","SWEPT_FACE",FACE,{"disambiguationData":[OSD([sQuery(id+"F121.wireOp",EDGE,"E226")])]})])],"derivedFrom":makeQuery(id+"F49.opExtrude","CAP_EDGE",EDGE,{"disambiguationData":[OSD([subQ0])],"isStart":false})});}
            var Q1;
            {var subQ0=sQuery(id+"F45.wireOp",EDGE,"E126.MirrorCS");var subQ1=sQuery(id+"F45.wireOp",EDGE,"E125.MirrorCS");var subQ2=sQuery(id+"F45.wireOp",EDGE,"E124");Q1=makeQuery(id+"F122.boolean.opBoolean","SPLIT",EDGE,{"disambiguationData":[TD([makeQuery(id+"F49.opExtrude","CAP_FACE",FACE,{"disambiguationData":[OSD([sQuery(id+"F45.wireOp",EDGE,"E123"),subQ2,subQ1,subQ0])],"isStart":false}),makeQuery(id+"F49.opExtrude","SWEPT_FACE",FACE,{"disambiguationData":[OSD([subQ2,subQ0])]}),makeQuery(id+"F49.opExtrude","SWEPT_FACE",FACE,{"disambiguationData":[OSD([subQ1])]}),makeQuery(id+"F122.opExtrude","SWEPT_FACE",FACE,{"disambiguationData":[OSD([sQuery(id+"F121.wireOp",EDGE,"E227.MirrorCS")])]})])],"derivedFrom":makeQuery(id+"F49.opExtrude","CAP_EDGE",EDGE,{"disambiguationData":[OSD([subQ1])],"isStart":false})});}
            fillet(context, id + "F124", {"entities" : qUnion([Q0, Q1]), "radius" : 0.2 * mm, "tangentPropagation" : true, "allowEdgeOverflow" : false});
        }
    });
